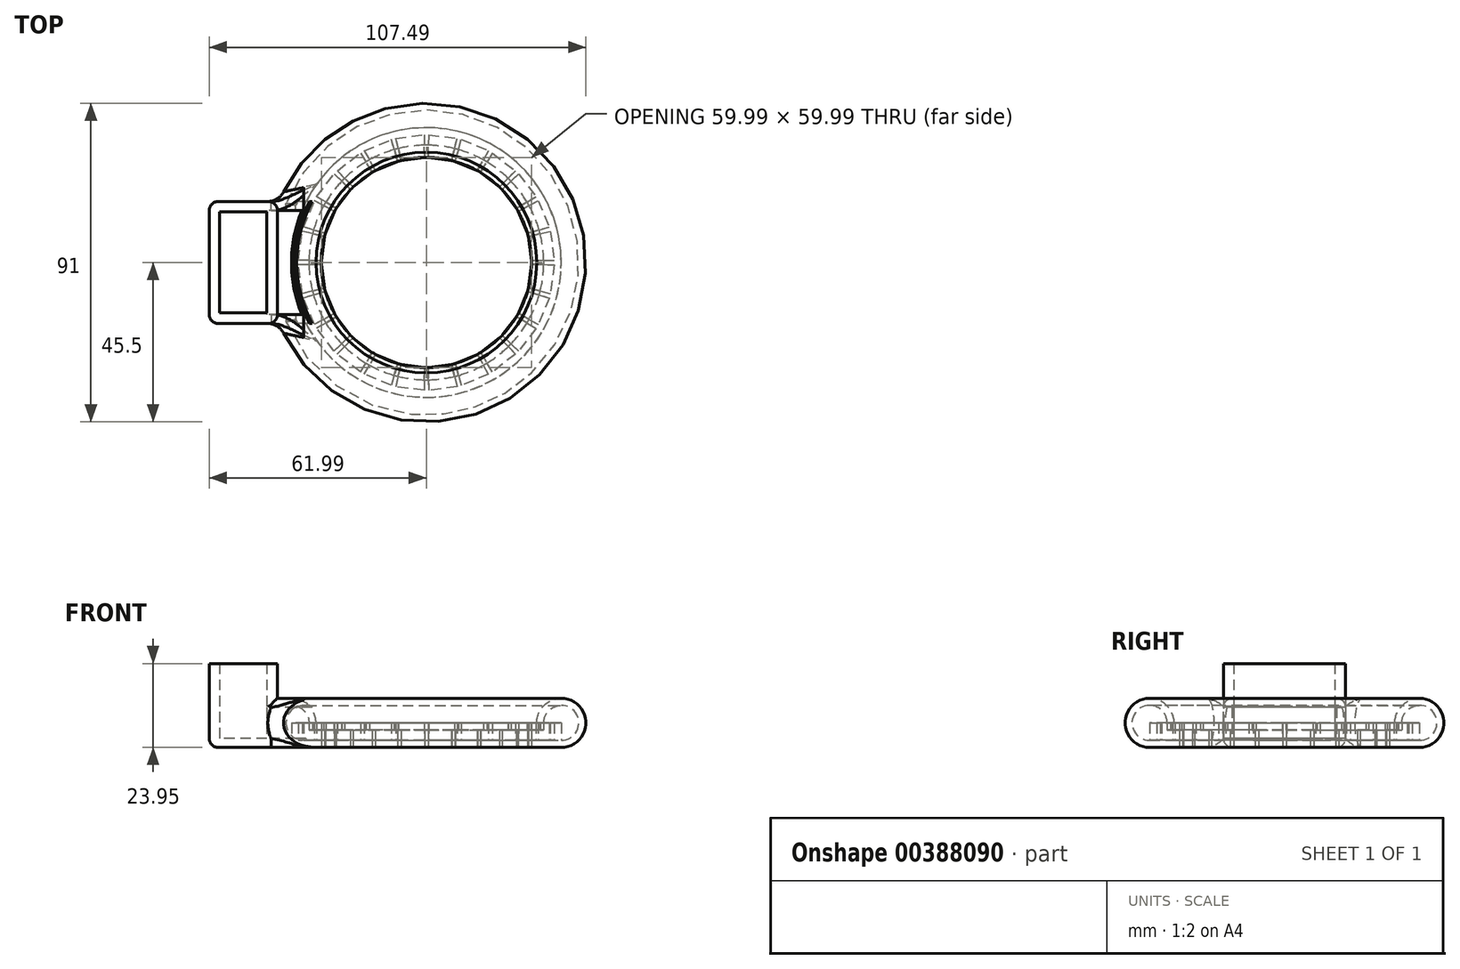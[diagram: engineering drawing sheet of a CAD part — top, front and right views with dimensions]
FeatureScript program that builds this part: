
annotation { "Feature Type Name" : "Feature", "Feature Type Description" : "" }
export const myFeature = defineFeature(function(context is Context, id is Id, definition is map)
    precondition{}
    {
        {
            var Q0;
            Q0=qCreatedBy(makeId("Right.planeOp"),FACE);
            cPlane(context, id + "F0", {"entities" : qUnion([Q0]), "cplaneType" : CPlaneType.OFFSET, "offset" : 45.5 * mm, "width" : 150 * mm, "height" : 150 * mm});
        }
        {
            var Q0;
            Q0=qCreatedBy(makeId("Front.planeOp"),FACE);
            cPlane(context, id + "F1", {"entities" : qUnion([Q0]), "cplaneType" : CPlaneType.OFFSET, "offset" : 17.41 * mm, "width" : 150 * mm, "height" : 150 * mm});
        }
        {
            var Q0;
            Q0=qCreatedBy(makeId("Front.planeOp"),FACE);
            cPlane(context, id + "F2", {"entities" : qUnion([Q0]), "cplaneType" : CPlaneType.OFFSET, "offset" : 17.41 * mm, "oppositeDirection" : true, "width" : 150 * mm, "height" : 150 * mm});
        }
        {
            var Q0;
            Q0=qCreatedBy(makeId("Top.planeOp"),FACE);
            cPlane(context, id + "F3", {"entities" : qUnion([Q0]), "cplaneType" : CPlaneType.OFFSET, "offset" : 7 * mm, "width" : 150 * mm, "height" : 150 * mm});
        }
        {
            var Q0;
            Q0=qCreatedBy(id+"F3.planeOp",FACE);
            cPlane(context, id + "F4", {"entities" : qUnion([Q0]), "cplaneType" : CPlaneType.OFFSET, "offset" : 6.95 * mm, "width" : 150 * mm, "height" : 150 * mm});
        }
        {
            var Q0;
            Q0=qCreatedBy(makeId("Top.planeOp"),FACE);
            var sketch = newSketch(context, id + "F5", { "sketchPlane" : qUnion([Q0])});
            skCircle(sketch, "E0", {"center": v(0, 0) * mm, "radius": 45 * mm});
            skCircle(sketch, "E1.0", {"center": v(0, 0) * mm, "radius": 38.5 * mm});
            skLineSegment(sketch, "E2", {"start": v(-136.41, 41.5) * mm, "end": v(-136.41, 35) * mm});
            skLineSegment(sketch, "E3", {"start": v(-128.72, 34) * mm, "end": v(-127.05, 40.28) * mm});
            skLineSegment(sketch, "E4", {"start": v(-118.16, 36.6) * mm, "end": v(-121.4, 30.99) * mm});
            skLineSegment(sketch, "E5", {"start": v(-115.15, 26.17) * mm, "end": v(-110.55, 30.76) * mm});
            skLineSegment(sketch, "E6", {"start": v(-110.44, 20.01) * mm, "end": v(-104.8, 23.26) * mm});
            skLineSegment(sketch, "E7", {"start": v(-107.45, 12.84) * mm, "end": v(-101.18, 14.54) * mm});
            skLineSegment(sketch, "E8", {"start": v(-106.41, 5.01) * mm, "end": v(-99.91, 5.01) * mm});
            skLineSegment(sketch, "E9.MirrorCS", {"start": v(-107.44, -2.81) * mm, "end": v(-101.17, -4.5) * mm});
            skLineSegment(sketch, "E10.MirrorCS", {"start": v(-110.42, -9.99) * mm, "end": v(-104.8, -13.24) * mm});
            skLineSegment(sketch, "E11.MirrorCS", {"start": v(-115.13, -16.15) * mm, "end": v(-110.52, -20.73) * mm});
            skLineSegment(sketch, "E12.MirrorCS", {"start": v(-118.13, -26.6) * mm, "end": v(-121.38, -20.97) * mm});
            skLineSegment(sketch, "E13.MirrorCS", {"start": v(-128.7, -24) * mm, "end": v(-127.02, -30.27) * mm});
            skLineSegment(sketch, "E14.MirrorCS", {"start": v(-144.1, 34) * mm, "end": v(-145.77, 40.28) * mm});
            skLineSegment(sketch, "E15.MirrorCS", {"start": v(-154.66, 36.6) * mm, "end": v(-151.41, 30.99) * mm});
            skLineSegment(sketch, "E16.MirrorCS", {"start": v(-157.67, 26.17) * mm, "end": v(-162.27, 30.76) * mm});
            skLineSegment(sketch, "E17.MirrorCS", {"start": v(-162.38, 20.01) * mm, "end": v(-168.01, 23.26) * mm});
            skLineSegment(sketch, "E18.MirrorCS", {"start": v(-165.37, 12.84) * mm, "end": v(-171.64, 14.54) * mm});
            skLineSegment(sketch, "E19.MirrorCS", {"start": v(-165.38, -2.81) * mm, "end": v(-171.65, -4.5) * mm});
            skLineSegment(sketch, "E20.MirrorCS", {"start": v(-162.4, -9.99) * mm, "end": v(-168.03, -13.24) * mm});
            skLineSegment(sketch, "E21.MirrorCS", {"start": v(-157.69, -16.15) * mm, "end": v(-162.3, -20.73) * mm});
            skLineSegment(sketch, "E22.MirrorCS", {"start": v(-154.69, -26.6) * mm, "end": v(-151.44, -20.97) * mm});
            skLineSegment(sketch, "E23.MirrorCS", {"start": v(-144.13, -24) * mm, "end": v(-145.8, -30.27) * mm});
            skLineSegment(sketch, "E24", {"start": v(-136.41, -25) * mm, "end": v(-136.41, -31.5) * mm});
            skLineSegment(sketch, "E25", {"start": v(-166.41, 5) * mm, "end": v(-172.91, 5) * mm});
            skCircle(sketch, "E26", {"center": v(-136.41, 5) * mm, "radius": 1.25 * mm, "construction": true});
            skLineSegment(sketch, "E27", {"start": v(0.64, 36.5) * mm, "end": v(0.52, 30) * mm});
            skLineSegment(sketch, "E28", {"start": v(8.2, 28.86) * mm, "end": v(9.97, 35.11) * mm});
            skLineSegment(sketch, "E29", {"start": v(18.8, 31.29) * mm, "end": v(15.46, 25.72) * mm});
            skLineSegment(sketch, "E30", {"start": v(21.62, 20.8) * mm, "end": v(26.3, 25.3) * mm});
            skLineSegment(sketch, "E31", {"start": v(26.23, 14.56) * mm, "end": v(31.92, 17.71) * mm});
            skLineSegment(sketch, "E32", {"start": v(29.1, 7.33) * mm, "end": v(35.4, 8.92) * mm});
            skLineSegment(sketch, "E33", {"start": v(30, -0.5) * mm, "end": v(36.5, -0.62) * mm});
            skLineSegment(sketch, "E34.MirrorCS", {"start": v(28.82, -8.32) * mm, "end": v(35.07, -10.12) * mm});
            skLineSegment(sketch, "E35.MirrorCS", {"start": v(25.72, -15.44) * mm, "end": v(31.3, -18.78) * mm});
            skLineSegment(sketch, "E36.MirrorCS", {"start": v(20.9, -21.52) * mm, "end": v(25.43, -26.18) * mm});
            skLineSegment(sketch, "E37.MirrorCS", {"start": v(17.73, -31.9) * mm, "end": v(14.57, -26.23) * mm});
            skLineSegment(sketch, "E38.MirrorCS", {"start": v(7.21, -29.12) * mm, "end": v(8.77, -35.43) * mm});
            skLineSegment(sketch, "E39.MirrorCS", {"start": v(-7.18, 29.13) * mm, "end": v(-8.74, 35.44) * mm});
            skLineSegment(sketch, "E40.MirrorCS", {"start": v(-17.7, 31.92) * mm, "end": v(-14.55, 26.25) * mm});
            skLineSegment(sketch, "E41.MirrorCS", {"start": v(-20.88, 21.54) * mm, "end": v(-25.4, 26.2) * mm});
            skLineSegment(sketch, "E42.MirrorCS", {"start": v(-25.7, 15.46) * mm, "end": v(-31.28, 18.81) * mm});
            skLineSegment(sketch, "E43.MirrorCS", {"start": v(-28.82, 8.34) * mm, "end": v(-35.06, 10.15) * mm});
            skLineSegment(sketch, "E44.MirrorCS", {"start": v(-29.1, -7.3) * mm, "end": v(-35.4, -8.89) * mm});
            skLineSegment(sketch, "E45.MirrorCS", {"start": v(-26.25, -14.53) * mm, "end": v(-31.93, -17.68) * mm});
            skLineSegment(sketch, "E46.MirrorCS", {"start": v(-21.64, -20.77) * mm, "end": v(-26.33, -25.28) * mm});
            skLineSegment(sketch, "E47.MirrorCS", {"start": v(-18.83, -31.27) * mm, "end": v(-15.48, -25.7) * mm});
            skLineSegment(sketch, "E48.MirrorCS", {"start": v(-8.22, -28.85) * mm, "end": v(-10, -35.1) * mm});
            skLineSegment(sketch, "E49", {"start": v(-0.52, -30) * mm, "end": v(-0.64, -36.5) * mm});
            skLineSegment(sketch, "E50", {"start": v(-30, 0.52) * mm, "end": v(-36.5, 0.64) * mm});
            skLineSegment(sketch, "E51", {"start": v(-0.64, 36.5) * mm, "end": v(-0.52, 30) * mm});
            skLineSegment(sketch, "E52", {"start": v(7.18, 29.13) * mm, "end": v(8.74, 35.44) * mm});
            skLineSegment(sketch, "E53", {"start": v(17.7, 31.92) * mm, "end": v(14.55, 26.25) * mm});
            skLineSegment(sketch, "E54", {"start": v(20.88, 21.54) * mm, "end": v(25.4, 26.2) * mm});
            skLineSegment(sketch, "E55", {"start": v(25.7, 15.46) * mm, "end": v(31.28, 18.81) * mm});
            skLineSegment(sketch, "E56", {"start": v(28.82, 8.34) * mm, "end": v(35.06, 10.15) * mm});
            skLineSegment(sketch, "E57", {"start": v(30, 0.54) * mm, "end": v(36.5, 0.65) * mm});
            skLineSegment(sketch, "E58.MirrorCS", {"start": v(29.1, -7.3) * mm, "end": v(35.4, -8.89) * mm});
            skLineSegment(sketch, "E59.MirrorCS", {"start": v(26.25, -14.53) * mm, "end": v(31.93, -17.68) * mm});
            skLineSegment(sketch, "E60.MirrorCS", {"start": v(21.64, -20.77) * mm, "end": v(26.33, -25.28) * mm});
            skLineSegment(sketch, "E61.MirrorCS", {"start": v(18.83, -31.27) * mm, "end": v(15.48, -25.7) * mm});
            skLineSegment(sketch, "E62.MirrorCS", {"start": v(8.22, -28.85) * mm, "end": v(10, -35.1) * mm});
            skLineSegment(sketch, "E63.MirrorCS", {"start": v(-8.2, 28.86) * mm, "end": v(-9.97, 35.11) * mm});
            skLineSegment(sketch, "E64.MirrorCS", {"start": v(-18.8, 31.29) * mm, "end": v(-15.46, 25.72) * mm});
            skLineSegment(sketch, "E65.MirrorCS", {"start": v(-21.62, 20.8) * mm, "end": v(-26.3, 25.3) * mm});
            skLineSegment(sketch, "E66.MirrorCS", {"start": v(-26.23, 14.56) * mm, "end": v(-31.92, 17.71) * mm});
            skLineSegment(sketch, "E67.MirrorCS", {"start": v(-29.1, 7.33) * mm, "end": v(-35.4, 8.92) * mm});
            skLineSegment(sketch, "E68.MirrorCS", {"start": v(-28.82, -8.32) * mm, "end": v(-35.07, -10.12) * mm});
            skLineSegment(sketch, "E69.MirrorCS", {"start": v(-25.72, -15.44) * mm, "end": v(-31.3, -18.78) * mm});
            skLineSegment(sketch, "E70.MirrorCS", {"start": v(-20.9, -21.52) * mm, "end": v(-25.43, -26.18) * mm});
            skLineSegment(sketch, "E71.MirrorCS", {"start": v(-17.73, -31.9) * mm, "end": v(-14.57, -26.23) * mm});
            skLineSegment(sketch, "E72.MirrorCS", {"start": v(-7.21, -29.12) * mm, "end": v(-8.77, -35.43) * mm});
            skLineSegment(sketch, "E73", {"start": v(0.52, -30) * mm, "end": v(0.64, -36.5) * mm});
            skLineSegment(sketch, "E74", {"start": v(-30, -0.52) * mm, "end": v(-36.5, -0.64) * mm});
            skCircle(sketch, "E75", {"center": v(0, 0) * mm, "radius": 1.25 * mm, "construction": true});
            skLineSegment(sketch, "E76", {"start": v(-29.1, 7.33) * mm, "end": v(-28.82, 8.34) * mm});
            skLineSegment(sketch, "E77", {"start": v(-28.82, 8.34) * mm, "end": v(-26.23, 14.56) * mm});
            skLineSegment(sketch, "E78", {"start": v(-26.23, 14.56) * mm, "end": v(-25.7, 15.46) * mm});
            skLineSegment(sketch, "E79", {"start": v(-25.7, 15.46) * mm, "end": v(-21.62, 20.8) * mm});
            skLineSegment(sketch, "E80", {"start": v(-21.62, 20.8) * mm, "end": v(-20.88, 21.54) * mm});
            skLineSegment(sketch, "E81", {"start": v(-20.88, 21.54) * mm, "end": v(-15.46, 25.72) * mm});
            skLineSegment(sketch, "E82", {"start": v(-15.46, 25.72) * mm, "end": v(-14.55, 26.25) * mm});
            skLineSegment(sketch, "E83", {"start": v(-14.55, 26.25) * mm, "end": v(-8.2, 28.86) * mm});
            skLineSegment(sketch, "E84", {"start": v(-8.2, 28.86) * mm, "end": v(-7.18, 29.13) * mm});
            skLineSegment(sketch, "E85", {"start": v(-7.18, 29.13) * mm, "end": v(-0.52, 30) * mm});
            skLineSegment(sketch, "E86", {"start": v(-0.52, 30) * mm, "end": v(0.52, 30) * mm});
            skLineSegment(sketch, "E87", {"start": v(0.52, 30) * mm, "end": v(7.18, 29.13) * mm});
            skLineSegment(sketch, "E88", {"start": v(7.18, 29.13) * mm, "end": v(8.2, 28.86) * mm});
            skLineSegment(sketch, "E89", {"start": v(8.2, 28.86) * mm, "end": v(14.55, 26.25) * mm});
            skLineSegment(sketch, "E90", {"start": v(14.55, 26.25) * mm, "end": v(15.46, 25.72) * mm});
            skLineSegment(sketch, "E91", {"start": v(15.46, 25.72) * mm, "end": v(20.88, 21.54) * mm});
            skLineSegment(sketch, "E92", {"start": v(20.88, 21.54) * mm, "end": v(21.62, 20.8) * mm});
            skLineSegment(sketch, "E93", {"start": v(21.62, 20.8) * mm, "end": v(25.7, 15.46) * mm});
            skLineSegment(sketch, "E94", {"start": v(25.7, 15.46) * mm, "end": v(26.23, 14.56) * mm});
            skLineSegment(sketch, "E95", {"start": v(26.23, 14.56) * mm, "end": v(28.82, 8.34) * mm});
            skLineSegment(sketch, "E96", {"start": v(28.82, 8.34) * mm, "end": v(29.1, 7.33) * mm});
            skLineSegment(sketch, "E97", {"start": v(29.1, 7.33) * mm, "end": v(30, 0.54) * mm});
            skLineSegment(sketch, "E98", {"start": v(30, 0.54) * mm, "end": v(30, -0.5) * mm});
            skLineSegment(sketch, "E99", {"start": v(30, -0.5) * mm, "end": v(29.1, -7.3) * mm});
            skLineSegment(sketch, "E100", {"start": v(29.1, -7.3) * mm, "end": v(28.82, -8.32) * mm});
            skLineSegment(sketch, "E101", {"start": v(28.82, -8.32) * mm, "end": v(26.25, -14.53) * mm});
            skLineSegment(sketch, "E102", {"start": v(26.25, -14.53) * mm, "end": v(25.72, -15.44) * mm});
            skLineSegment(sketch, "E103", {"start": v(25.72, -15.44) * mm, "end": v(21.64, -20.77) * mm});
            skLineSegment(sketch, "E104", {"start": v(21.64, -20.77) * mm, "end": v(20.9, -21.52) * mm});
            skLineSegment(sketch, "E105", {"start": v(20.9, -21.52) * mm, "end": v(15.48, -25.7) * mm});
            skLineSegment(sketch, "E106", {"start": v(15.48, -25.7) * mm, "end": v(14.57, -26.23) * mm});
            skLineSegment(sketch, "E107", {"start": v(14.57, -26.23) * mm, "end": v(8.22, -28.85) * mm});
            skLineSegment(sketch, "E108", {"start": v(8.22, -28.85) * mm, "end": v(7.21, -29.12) * mm});
            skLineSegment(sketch, "E109", {"start": v(7.21, -29.12) * mm, "end": v(0.52, -30) * mm});
            skLineSegment(sketch, "E110", {"start": v(0.52, -30) * mm, "end": v(-0.52, -30) * mm});
            skLineSegment(sketch, "E111", {"start": v(-0.52, -30) * mm, "end": v(-7.21, -29.12) * mm});
            skLineSegment(sketch, "E112", {"start": v(-7.21, -29.12) * mm, "end": v(-8.22, -28.85) * mm});
            skLineSegment(sketch, "E113", {"start": v(-8.22, -28.85) * mm, "end": v(-14.57, -26.23) * mm});
            skLineSegment(sketch, "E114", {"start": v(-14.57, -26.23) * mm, "end": v(-15.48, -25.7) * mm});
            skLineSegment(sketch, "E115", {"start": v(-15.48, -25.7) * mm, "end": v(-20.9, -21.52) * mm});
            skLineSegment(sketch, "E116", {"start": v(-20.9, -21.52) * mm, "end": v(-21.64, -20.77) * mm});
            skLineSegment(sketch, "E117", {"start": v(-21.64, -20.77) * mm, "end": v(-25.72, -15.44) * mm});
            skLineSegment(sketch, "E118", {"start": v(-25.72, -15.44) * mm, "end": v(-26.25, -14.53) * mm});
            skLineSegment(sketch, "E119", {"start": v(-28.82, -8.32) * mm, "end": v(-29.1, -7.3) * mm});
            skLineSegment(sketch, "E120", {"start": v(-26.25, -14.53) * mm, "end": v(-28.82, -8.32) * mm});
            skLineSegment(sketch, "E121", {"start": v(-29.1, -7.3) * mm, "end": v(-30, -0.52) * mm});
            skLineSegment(sketch, "E122", {"start": v(-30, -0.52) * mm, "end": v(-30, 0.52) * mm});
            skLineSegment(sketch, "E123", {"start": v(-30, 0.52) * mm, "end": v(-29.1, 7.33) * mm});
            skLineSegment(sketch, "E124", {"start": v(-36.5, 0.64) * mm, "end": v(-35.4, 8.92) * mm});
            skLineSegment(sketch, "E125", {"start": v(-35.06, 10.15) * mm, "end": v(-31.92, 17.71) * mm});
            skLineSegment(sketch, "E126", {"start": v(-31.28, 18.81) * mm, "end": v(-26.3, 25.3) * mm});
            skLineSegment(sketch, "E127", {"start": v(-25.4, 26.2) * mm, "end": v(-18.8, 31.29) * mm});
            skLineSegment(sketch, "E128", {"start": v(-17.7, 31.92) * mm, "end": v(-9.97, 35.11) * mm});
            skLineSegment(sketch, "E129", {"start": v(-8.74, 35.44) * mm, "end": v(-0.64, 36.5) * mm});
            skLineSegment(sketch, "E130", {"start": v(0.64, 36.5) * mm, "end": v(8.74, 35.44) * mm});
            skLineSegment(sketch, "E131", {"start": v(9.97, 35.11) * mm, "end": v(17.7, 31.92) * mm});
            skLineSegment(sketch, "E132", {"start": v(18.8, 31.29) * mm, "end": v(25.4, 26.2) * mm});
            skLineSegment(sketch, "E133", {"start": v(26.3, 25.3) * mm, "end": v(31.28, 18.81) * mm});
            skLineSegment(sketch, "E134", {"start": v(31.92, 17.71) * mm, "end": v(35.06, 10.15) * mm});
            skLineSegment(sketch, "E135", {"start": v(35.4, 8.92) * mm, "end": v(36.5, 0.65) * mm});
            skLineSegment(sketch, "E136", {"start": v(36.5, -0.62) * mm, "end": v(35.4, -8.89) * mm});
            skLineSegment(sketch, "E137", {"start": v(35.07, -10.12) * mm, "end": v(31.93, -17.68) * mm});
            skLineSegment(sketch, "E138", {"start": v(31.3, -18.78) * mm, "end": v(26.33, -25.28) * mm});
            skLineSegment(sketch, "E139", {"start": v(25.43, -26.18) * mm, "end": v(18.83, -31.27) * mm});
            skLineSegment(sketch, "E140", {"start": v(17.73, -31.9) * mm, "end": v(10, -35.1) * mm});
            skLineSegment(sketch, "E141", {"start": v(8.77, -35.43) * mm, "end": v(0.64, -36.5) * mm});
            skLineSegment(sketch, "E142", {"start": v(-0.64, -36.5) * mm, "end": v(-8.77, -35.43) * mm});
            skLineSegment(sketch, "E143", {"start": v(-10, -35.1) * mm, "end": v(-17.73, -31.9) * mm});
            skLineSegment(sketch, "E144", {"start": v(-18.83, -31.27) * mm, "end": v(-25.43, -26.18) * mm});
            skLineSegment(sketch, "E145", {"start": v(-26.33, -25.28) * mm, "end": v(-31.3, -18.78) * mm});
            skLineSegment(sketch, "E146", {"start": v(-31.93, -17.68) * mm, "end": v(-35.07, -10.12) * mm});
            skLineSegment(sketch, "E147", {"start": v(-35.4, -8.89) * mm, "end": v(-36.5, -0.64) * mm});
            skSolve(sketch);
        }
        {
            var Q0;
            Q0=qCreatedBy(makeId("Front.planeOp"),FACE);
            var sketch = newSketch(context, id + "F6", { "sketchPlane" : qUnion([Q0])});
            skLineSegment(sketch, "E148.bottom", {"start": v(38.5, 7) * mm, "end": v(-38.5, 7) * mm, "construction": true});
            skLineSegment(sketch, "E148.top", {"start": v(38.5, -7) * mm, "end": v(-38.5, -7) * mm, "construction": true});
            skLineSegment(sketch, "E148.left", {"start": v(38.5, 7) * mm, "end": v(38.5, -7) * mm, "construction": true});
            skLineSegment(sketch, "E148.right", {"start": v(-38.5, 7) * mm, "end": v(-38.5, -7) * mm, "construction": true});
            skPoint(sketch, "E148.middle", {"position": v(0, 0) * mm});
            skLineSegment(sketch, "E149", {"start": v(-38.5, 0) * mm, "end": v(38.5, 0) * mm, "construction": true});
            skArc(sketch, "E150", {"start": v(38.5, 0) * mm, "mid": v(43.45, 11.95) * mm, "end": v(31.5, 7) * mm});
            skArc(sketch, "E151", {"start": v(38.5, 2) * mm, "mid": v(42.04, 10.54) * mm, "end": v(33.5, 7) * mm});
            skLineSegment(sketch, "E152", {"start": v(38.5, 2) * mm, "end": v(38.5, 0) * mm});
            skLineSegment(sketch, "E153", {"start": v(38.5, 2) * mm, "end": v(31.5, 2) * mm, "construction": true});
            skLineSegment(sketch, "E154", {"start": v(31.5, 2) * mm, "end": v(31.5, 0) * mm, "construction": true});
            skLineSegment(sketch, "E155.0", {"start": v(38.5, 5) * mm, "end": v(-38.5, 5) * mm, "construction": true});
            skLineSegment(sketch, "E156", {"start": v(30, 0) * mm, "end": v(30, 7) * mm, "construction": true});
            skLineSegment(sketch, "E157", {"start": v(31.5, 7) * mm, "end": v(30, 7) * mm});
            skLineSegment(sketch, "E158", {"start": v(30, 7) * mm, "end": v(30, 5) * mm});
            skLineSegment(sketch, "E159", {"start": v(30, 5) * mm, "end": v(33.5, 5) * mm});
            skLineSegment(sketch, "E160", {"start": v(33.5, 5) * mm, "end": v(33.5, 7) * mm});
            skLineSegment(sketch, "E161", {"start": v(0, -7) * mm, "end": v(0, 7) * mm, "construction": true});
            skLineSegment(sketch, "E162", {"start": v(38.5, 7) * mm, "end": v(38.5, 14) * mm, "construction": true});
            skLineSegment(sketch, "E163", {"start": v(38.5, 7) * mm, "end": v(45.5, 7) * mm, "construction": true});
            skLineSegment(sketch, "E164", {"start": v(38.5, 12) * mm, "end": v(38.5, 14) * mm});
            skLineSegment(sketch, "E165", {"start": v(43.5, 7) * mm, "end": v(45.5, 7) * mm});
            skLineSegment(sketch, "E166.MirrorCS", {"start": v(-38.5, 2) * mm, "end": v(-38.5, 0) * mm});
            skLineSegment(sketch, "E167.MirrorCS", {"start": v(-30, 7) * mm, "end": v(-30, 5) * mm});
            skLineSegment(sketch, "E168.MirrorCS", {"start": v(-31.5, 7) * mm, "end": v(-30, 7) * mm});
            skLineSegment(sketch, "E169.MirrorCS", {"start": v(-33.5, 5) * mm, "end": v(-33.5, 7) * mm});
            skLineSegment(sketch, "E170.MirrorCS", {"start": v(-43.5, 7) * mm, "end": v(-45.5, 7) * mm});
            skLineSegment(sketch, "E171.MirrorCS", {"start": v(-30, 5) * mm, "end": v(-33.5, 5) * mm});
            skLineSegment(sketch, "E172.MirrorCS", {"start": v(-31.5, 2) * mm, "end": v(-31.5, 0) * mm, "construction": true});
            skLineSegment(sketch, "E173.MirrorCS", {"start": v(-38.5, 12) * mm, "end": v(-38.5, 14) * mm});
            skLineSegment(sketch, "E174.MirrorCS", {"start": v(-38.5, 7) * mm, "end": v(-45.5, 7) * mm, "construction": true});
            skLineSegment(sketch, "E175.MirrorCS", {"start": v(-38.5, 2) * mm, "end": v(-31.5, 2) * mm, "construction": true});
            skLineSegment(sketch, "E176.MirrorCS", {"start": v(-38.5, 7) * mm, "end": v(-38.5, 14) * mm, "construction": true});
            skArc(sketch, "E177.MirrorCS", {"start": v(-38.5, 0) * mm, "mid": v(-43.45, 11.95) * mm, "end": v(-31.5, 7) * mm});
            skArc(sketch, "E178.MirrorCS", {"start": v(-38.5, 2) * mm, "mid": v(-42.04, 10.54) * mm, "end": v(-33.5, 7) * mm});
            skLineSegment(sketch, "E179.MirrorCS", {"start": v(-38.5, 5) * mm, "end": v(38.5, 5) * mm, "construction": true});
            skLineSegment(sketch, "E180.MirrorCS", {"start": v(-30, 0) * mm, "end": v(-30, 7) * mm, "construction": true});
            skLineSegment(sketch, "E181.MirrorCS", {"start": v(-38.5, 7) * mm, "end": v(38.5, 7) * mm, "construction": true});
            skSolve(sketch);
        }
        {
            var Q0;
            Q0=qCreatedBy(id+"F1.planeOp",FACE);
            var sketch = newSketch(context, id + "F7", { "sketchPlane" : qUnion([Q0])});
            skLineSegment(sketch, "E182.bottom", {"start": v(45.5, 14) * mm, "end": v(-45.5, 14) * mm, "construction": true});
            skLineSegment(sketch, "E182.top", {"start": v(45.5, -14) * mm, "end": v(-45.5, -14) * mm, "construction": true});
            skLineSegment(sketch, "E182.left", {"start": v(45.5, 14) * mm, "end": v(45.5, -14) * mm, "construction": true});
            skLineSegment(sketch, "E182.right", {"start": v(-45.5, 14) * mm, "end": v(-45.5, -14) * mm, "construction": true});
            skPoint(sketch, "E182.middle", {"position": v(0, 0) * mm});
            skLineSegment(sketch, "E183", {"start": v(-45.5, 0) * mm, "end": v(45.5, 0) * mm, "construction": true});
            skLineSegment(sketch, "E184", {"start": v(0, 14) * mm, "end": v(0, -14) * mm, "construction": true});
            skLineSegment(sketch, "E185.0", {"start": v(-17.41, 14) * mm, "end": v(-17.41, -14) * mm, "construction": true});
            skLineSegment(sketch, "E186.MirrorCS", {"start": v(17.41, 14) * mm, "end": v(17.41, -14) * mm, "construction": true});
            skLineSegment(sketch, "E187.0", {"start": v(45.5, 7) * mm, "end": v(-45.5, 7) * mm, "construction": true});
            skLineSegment(sketch, "E188", {"start": v(-17.41, 14) * mm, "end": v(-17.41, 7) * mm});
            skLineSegment(sketch, "E189", {"start": v(-17.41, 7) * mm, "end": v(17.41, 7) * mm});
            skLineSegment(sketch, "E190", {"start": v(17.41, 7) * mm, "end": v(17.41, 14) * mm});
            skLineSegment(sketch, "E191", {"start": v(17.41, 14) * mm, "end": v(-17.41, 14) * mm});
            skLineSegment(sketch, "E192.0", {"start": v(45.5, 12) * mm, "end": v(-45.5, 12) * mm, "construction": true});
            skLineSegment(sketch, "E193.0", {"start": v(-14.73, 14) * mm, "end": v(-14.73, -14) * mm, "construction": true});
            skLineSegment(sketch, "E194.MirrorCS", {"start": v(14.73, 14) * mm, "end": v(14.73, -14) * mm, "construction": true});
            skLineSegment(sketch, "E195", {"start": v(-14.73, 7) * mm, "end": v(-14.73, 14) * mm});
            skLineSegment(sketch, "E196", {"start": v(14.73, 7) * mm, "end": v(14.73, 14) * mm});
            skLineSegment(sketch, "E197", {"start": v(17.41, 12) * mm, "end": v(-17.41, 12) * mm});
            skPoint(sketch, "E197.startSnap0", {"position": v(17.41, 10.5) * mm});
            skLineSegment(sketch, "E198", {"start": v(45.5, 14) * mm, "end": v(45.5, 7) * mm});
            skCircle(sketch, "E199", {"center": v(-35.07, 7) * mm, "radius": 7 * mm, "construction": true});
            skArc(sketch, "E200", {"start": v(-35.07, 12) * mm, "mid": v(-40.07, 7) * mm, "end": v(-35.07, 2) * mm});
            skLineSegment(sketch, "E201", {"start": v(-35.07, 12) * mm, "end": v(-35.07, 14) * mm});
            skLineSegment(sketch, "E202", {"start": v(-35.07, 14) * mm, "end": v(-45.5, 14) * mm});
            skLineSegment(sketch, "E203", {"start": v(-45.5, 14) * mm, "end": v(-45.5, 0) * mm});
            skLineSegment(sketch, "E204", {"start": v(-45.5, 0) * mm, "end": v(-35.07, 0) * mm});
            skLineSegment(sketch, "E205", {"start": v(-35.07, 0) * mm, "end": v(-35.07, 2) * mm});
            skLineSegment(sketch, "E206.MirrorCS", {"start": v(45.5, 2) * mm, "end": v(-45.5, 2) * mm, "construction": true});
            skCircle(sketch, "E207", {"center": v(0, 7) * mm, "radius": 1.25 * mm, "construction": true});
            skSolve(sketch);
        }
        {
            var Q0;
            Q0=qCreatedBy(id+"F2.planeOp",FACE);
            var sketch = newSketch(context, id + "F8", { "sketchPlane" : qUnion([Q0])});
            skLineSegment(sketch, "E208.bottom", {"start": v(45.5, 14) * mm, "end": v(-45.5, 14) * mm, "construction": true});
            skLineSegment(sketch, "E208.top", {"start": v(45.5, -14) * mm, "end": v(-45.5, -14) * mm, "construction": true});
            skLineSegment(sketch, "E208.left", {"start": v(45.5, 14) * mm, "end": v(45.5, -14) * mm, "construction": true});
            skLineSegment(sketch, "E208.right", {"start": v(-45.5, 14) * mm, "end": v(-45.5, -14) * mm, "construction": true});
            skPoint(sketch, "E208.middle", {"position": v(0, 0) * mm});
            skLineSegment(sketch, "E209", {"start": v(-45.5, 0) * mm, "end": v(45.5, 0) * mm, "construction": true});
            skLineSegment(sketch, "E210", {"start": v(0, 14) * mm, "end": v(0, -14) * mm, "construction": true});
            skLineSegment(sketch, "E211.0", {"start": v(-17.41, 14) * mm, "end": v(-17.41, -14) * mm, "construction": true});
            skLineSegment(sketch, "E212.MirrorCS", {"start": v(17.41, 14) * mm, "end": v(17.41, -14) * mm, "construction": true});
            skLineSegment(sketch, "E213.0", {"start": v(45.5, 7) * mm, "end": v(-45.5, 7) * mm, "construction": true});
            skLineSegment(sketch, "E214", {"start": v(-17.41, 14) * mm, "end": v(-17.41, 7) * mm});
            skLineSegment(sketch, "E215", {"start": v(-17.41, 7) * mm, "end": v(17.41, 7) * mm});
            skLineSegment(sketch, "E216", {"start": v(17.41, 7) * mm, "end": v(17.41, 14) * mm});
            skLineSegment(sketch, "E217", {"start": v(17.41, 14) * mm, "end": v(-17.41, 14) * mm});
            skLineSegment(sketch, "E218.0", {"start": v(45.5, 12) * mm, "end": v(-45.5, 12) * mm, "construction": true});
            skLineSegment(sketch, "E219.0", {"start": v(-14.73, 14) * mm, "end": v(-14.73, -14) * mm, "construction": true});
            skLineSegment(sketch, "E220.MirrorCS", {"start": v(14.73, 14) * mm, "end": v(14.73, -14) * mm, "construction": true});
            skLineSegment(sketch, "E221", {"start": v(-14.73, 7) * mm, "end": v(-14.73, 14) * mm});
            skLineSegment(sketch, "E222", {"start": v(14.73, 7) * mm, "end": v(14.73, 14) * mm});
            skLineSegment(sketch, "E223", {"start": v(17.41, 12) * mm, "end": v(-17.41, 12) * mm});
            skPoint(sketch, "E223.startSnap0", {"position": v(17.41, 10.5) * mm});
            skLineSegment(sketch, "E224", {"start": v(45.5, 14) * mm, "end": v(45.5, 7) * mm});
            skCircle(sketch, "E225", {"center": v(-35.07, 7) * mm, "radius": 7 * mm, "construction": true});
            skArc(sketch, "E226", {"start": v(-35.07, 12) * mm, "mid": v(-40.07, 7) * mm, "end": v(-35.07, 2) * mm});
            skLineSegment(sketch, "E227", {"start": v(-35.07, 12) * mm, "end": v(-35.07, 14) * mm});
            skLineSegment(sketch, "E228", {"start": v(-35.07, 14) * mm, "end": v(-45.5, 14) * mm});
            skLineSegment(sketch, "E229", {"start": v(-45.5, 14) * mm, "end": v(-45.5, 0) * mm});
            skLineSegment(sketch, "E230", {"start": v(-45.5, 0) * mm, "end": v(-35.07, 0) * mm});
            skLineSegment(sketch, "E231", {"start": v(-35.07, 0) * mm, "end": v(-35.07, 2) * mm});
            skLineSegment(sketch, "E232.MirrorCS", {"start": v(45.5, 2) * mm, "end": v(-45.5, 2) * mm, "construction": true});
            skCircle(sketch, "E233", {"center": v(0, 7) * mm, "radius": 1.25 * mm, "construction": true});
            skSolve(sketch);
        }
        {
            var Q0;
            Q0=qCreatedBy(makeId("Top.planeOp"),FACE);
            var sketch = newSketch(context, id + "F9", { "sketchPlane" : qUnion([Q0])});
            skPoint(sketch, "E234.middle", {"position": v(0, 0) * mm});
            skCircle(sketch, "E235", {"center": v(0, 0) * mm, "radius": 2.5 * mm, "construction": true});
            skLineSegment(sketch, "E236.MirrorCS", {"start": v(-32.65, 17.41) * mm, "end": v(-45.5, 17.41) * mm});
            skLineSegment(sketch, "E237.MirrorCS", {"start": v(-32.65, -17.41) * mm, "end": v(-45.5, -17.41) * mm});
            skLineSegment(sketch, "E238.MirrorCS", {"start": v(-45.5, 17.41) * mm, "end": v(-45.5, -17.41) * mm});
            skArc(sketch, "E239", {"start": v(-32.65, 17.41) * mm, "mid": v(-37, 0) * mm, "end": v(-32.65, -17.41) * mm});
            skLineSegment(sketch, "E240.bottom", {"start": v(-45.5, 8.28) * mm, "end": v(-45.5, -8.52) * mm, "construction": true});
            skLineSegment(sketch, "E240.left", {"start": v(-45.5, 8.28) * mm, "end": v(-59, 8.28) * mm, "construction": true});
            skLineSegment(sketch, "E241", {"start": v(-45.5, -8.52) * mm, "end": v(-59, -8.52) * mm, "construction": true});
            skLineSegment(sketch, "E242", {"start": v(-59, -8.52) * mm, "end": v(-59, 8.28) * mm, "construction": true});
            skLineSegment(sketch, "E243", {"start": v(-45.5, 8.28) * mm, "end": v(-59, -8.52) * mm, "construction": true});
            skLineSegment(sketch, "E244", {"start": v(-45.5, -8.52) * mm, "end": v(-59, 8.28) * mm, "construction": true});
            skLineSegment(sketch, "E245", {"start": v(-52.24, 0) * mm, "end": v(-42.5, 0) * mm, "construction": true});
            skLineSegment(sketch, "E246", {"start": v(-27.2, 0) * mm, "end": v(-42.4, 0) * mm, "construction": true});
            skLineSegment(sketch, "E247.0", {"start": v(-62, -8.52) * mm, "end": v(-62, 8.28) * mm, "construction": true});
            skLineSegment(sketch, "E248", {"start": v(-45.5, 17.41) * mm, "end": v(-62, 17.41) * mm});
            skLineSegment(sketch, "E249", {"start": v(-62, 17.41) * mm, "end": v(-62, -17.41) * mm});
            skLineSegment(sketch, "E250", {"start": v(-62, -17.41) * mm, "end": v(-45.5, -17.41) * mm});
            skLineSegment(sketch, "E251.0", {"start": v(-59, -14.41) * mm, "end": v(-45.5, -14.41) * mm});
            skLineSegment(sketch, "E251.1", {"start": v(-59, 14.41) * mm, "end": v(-59, -14.41) * mm});
            skLineSegment(sketch, "E251.2", {"start": v(-45.5, 14.41) * mm, "end": v(-59, 14.41) * mm});
            skSolve(sketch);
        }
        {
            var Q0;
            Q0=qCreatedBy(id+"F4.planeOp",FACE);
            var sketch = newSketch(context, id + "F10", { "sketchPlane" : qUnion([Q0])});
            skPoint(sketch, "E252.middle", {"position": v(0, 0) * mm});
            skCircle(sketch, "E253", {"center": v(0, 0) * mm, "radius": 2.5 * mm, "construction": true});
            skLineSegment(sketch, "E254.MirrorCS", {"start": v(-32.65, 17.41) * mm, "end": v(-45.5, 17.41) * mm});
            skLineSegment(sketch, "E255.MirrorCS", {"start": v(-32.65, -17.41) * mm, "end": v(-45.5, -17.41) * mm});
            skLineSegment(sketch, "E256.MirrorCS", {"start": v(-45.5, 17.41) * mm, "end": v(-45.5, -17.41) * mm});
            skArc(sketch, "E257", {"start": v(-32.65, 17.41) * mm, "mid": v(-37, 0) * mm, "end": v(-32.65, -17.41) * mm});
            skLineSegment(sketch, "E258.bottom", {"start": v(-45.5, 8.28) * mm, "end": v(-45.5, -8.52) * mm, "construction": true});
            skLineSegment(sketch, "E258.left", {"start": v(-45.5, 8.28) * mm, "end": v(-59, 8.28) * mm, "construction": true});
            skLineSegment(sketch, "E259", {"start": v(-45.5, -8.52) * mm, "end": v(-59, -8.52) * mm, "construction": true});
            skLineSegment(sketch, "E260", {"start": v(-59, -8.52) * mm, "end": v(-59, 8.28) * mm, "construction": true});
            skLineSegment(sketch, "E261", {"start": v(-45.5, 8.28) * mm, "end": v(-59, -8.52) * mm, "construction": true});
            skLineSegment(sketch, "E262", {"start": v(-45.5, -8.52) * mm, "end": v(-59, 8.28) * mm, "construction": true});
            skLineSegment(sketch, "E263", {"start": v(-52.24, 0) * mm, "end": v(-42.5, 0) * mm, "construction": true});
            skLineSegment(sketch, "E264", {"start": v(-27.2, 0) * mm, "end": v(-42.4, 0) * mm, "construction": true});
            skLineSegment(sketch, "E265.0", {"start": v(-62, -8.52) * mm, "end": v(-62, 8.28) * mm, "construction": true});
            skLineSegment(sketch, "E266", {"start": v(-45.5, 17.41) * mm, "end": v(-62, 17.41) * mm});
            skLineSegment(sketch, "E267", {"start": v(-62, 17.41) * mm, "end": v(-62, -17.41) * mm});
            skLineSegment(sketch, "E268", {"start": v(-62, -17.41) * mm, "end": v(-45.5, -17.41) * mm});
            skLineSegment(sketch, "E269.0", {"start": v(-59, -14.41) * mm, "end": v(-45.5, -14.41) * mm});
            skLineSegment(sketch, "E269.1", {"start": v(-59, 14.41) * mm, "end": v(-59, -14.41) * mm});
            skLineSegment(sketch, "E269.2", {"start": v(-45.5, 14.41) * mm, "end": v(-59, 14.41) * mm});
            skLineSegment(sketch, "E270.0", {"start": v(-42.5, 17.41) * mm, "end": v(-42.5, -17.41) * mm});
            skSolve(sketch);
        }
        {
            var Q0;
            Q0=makeQuery(id+"F5.imprint","IMPRINT",FACE,{"disambiguationData":[TD([[makeQuery(id+"F5.imprint","IMPRINT",EDGE,{"derivedFrom":sQuery(id+"F5.wireOp",EDGE,"E1.0")}),1.0]])]});
            extrude(context, id + "F11", {"entities" : qUnion([Q0]), "depth" : 7 * mm});
        }
        {
            var Q0;
            Q0=makeQuery(id+"F5.imprint","IMPRINT",FACE,{"disambiguationData":[TD([[makeQuery(id+"F5.imprint","IMPRINT",EDGE,{"derivedFrom":sQuery(id+"F5.wireOp",EDGE,"E50")}),-1.0]])]});
            var Q1;
            Q1=makeQuery(id+"F5.imprint","IMPRINT",FACE,{"disambiguationData":[TD([[makeQuery(id+"F5.imprint","IMPRINT",EDGE,{"derivedFrom":sQuery(id+"F5.wireOp",EDGE,"E43.MirrorCS")}),-1.0]])]});
            var Q2;
            Q2=makeQuery(id+"F5.imprint","IMPRINT",FACE,{"disambiguationData":[TD([[makeQuery(id+"F5.imprint","IMPRINT",EDGE,{"derivedFrom":sQuery(id+"F5.wireOp",EDGE,"E42.MirrorCS")}),-1.0]])]});
            var Q3;
            Q3=makeQuery(id+"F5.imprint","IMPRINT",FACE,{"disambiguationData":[TD([[makeQuery(id+"F5.imprint","IMPRINT",EDGE,{"derivedFrom":sQuery(id+"F5.wireOp",EDGE,"E41.MirrorCS")}),-1.0]])]});
            var Q4;
            Q4=makeQuery(id+"F5.imprint","IMPRINT",FACE,{"disambiguationData":[TD([[makeQuery(id+"F5.imprint","IMPRINT",EDGE,{"derivedFrom":sQuery(id+"F5.wireOp",EDGE,"E40.MirrorCS")}),1.0]])]});
            var Q5;
            Q5=makeQuery(id+"F5.imprint","IMPRINT",FACE,{"disambiguationData":[TD([[makeQuery(id+"F5.imprint","IMPRINT",EDGE,{"derivedFrom":sQuery(id+"F5.wireOp",EDGE,"E39.MirrorCS")}),-1.0]])]});
            var Q6;
            Q6=makeQuery(id+"F5.imprint","IMPRINT",FACE,{"disambiguationData":[TD([[makeQuery(id+"F5.imprint","IMPRINT",EDGE,{"derivedFrom":sQuery(id+"F5.wireOp",EDGE,"E27")}),1.0]])]});
            var Q7;
            Q7=makeQuery(id+"F5.imprint","IMPRINT",FACE,{"disambiguationData":[TD([[makeQuery(id+"F5.imprint","IMPRINT",EDGE,{"derivedFrom":sQuery(id+"F5.wireOp",EDGE,"E28")}),-1.0]])]});
            var Q8;
            Q8=makeQuery(id+"F5.imprint","IMPRINT",FACE,{"disambiguationData":[TD([[makeQuery(id+"F5.imprint","IMPRINT",EDGE,{"derivedFrom":sQuery(id+"F5.wireOp",EDGE,"E29")}),1.0]])]});
            var Q9;
            Q9=makeQuery(id+"F5.imprint","IMPRINT",FACE,{"disambiguationData":[TD([[makeQuery(id+"F5.imprint","IMPRINT",EDGE,{"derivedFrom":sQuery(id+"F5.wireOp",EDGE,"E30")}),-1.0]])]});
            var Q10;
            Q10=makeQuery(id+"F5.imprint","IMPRINT",FACE,{"disambiguationData":[TD([[makeQuery(id+"F5.imprint","IMPRINT",EDGE,{"derivedFrom":sQuery(id+"F5.wireOp",EDGE,"E31")}),-1.0]])]});
            var Q11;
            Q11=makeQuery(id+"F5.imprint","IMPRINT",FACE,{"disambiguationData":[TD([[makeQuery(id+"F5.imprint","IMPRINT",EDGE,{"derivedFrom":sQuery(id+"F5.wireOp",EDGE,"E32")}),-1.0]])]});
            var Q12;
            Q12=makeQuery(id+"F5.imprint","IMPRINT",FACE,{"disambiguationData":[TD([[makeQuery(id+"F5.imprint","IMPRINT",EDGE,{"derivedFrom":sQuery(id+"F5.wireOp",EDGE,"E33")}),-1.0]])]});
            var Q13;
            Q13=makeQuery(id+"F5.imprint","IMPRINT",FACE,{"disambiguationData":[TD([[makeQuery(id+"F5.imprint","IMPRINT",EDGE,{"derivedFrom":sQuery(id+"F5.wireOp",EDGE,"E34.MirrorCS")}),-1.0]])]});
            var Q14;
            Q14=makeQuery(id+"F5.imprint","IMPRINT",FACE,{"disambiguationData":[TD([[makeQuery(id+"F5.imprint","IMPRINT",EDGE,{"derivedFrom":sQuery(id+"F5.wireOp",EDGE,"E35.MirrorCS")}),-1.0]])]});
            var Q15;
            Q15=makeQuery(id+"F5.imprint","IMPRINT",FACE,{"disambiguationData":[TD([[makeQuery(id+"F5.imprint","IMPRINT",EDGE,{"derivedFrom":sQuery(id+"F5.wireOp",EDGE,"E36.MirrorCS")}),-1.0]])]});
            var Q16;
            Q16=makeQuery(id+"F5.imprint","IMPRINT",FACE,{"disambiguationData":[TD([[makeQuery(id+"F5.imprint","IMPRINT",EDGE,{"derivedFrom":sQuery(id+"F5.wireOp",EDGE,"E37.MirrorCS")}),1.0]])]});
            var Q17;
            Q17=makeQuery(id+"F5.imprint","IMPRINT",FACE,{"disambiguationData":[TD([[makeQuery(id+"F5.imprint","IMPRINT",EDGE,{"derivedFrom":sQuery(id+"F5.wireOp",EDGE,"E38.MirrorCS")}),-1.0]])]});
            var Q18;
            Q18=makeQuery(id+"F5.imprint","IMPRINT",FACE,{"disambiguationData":[TD([[makeQuery(id+"F5.imprint","IMPRINT",EDGE,{"derivedFrom":sQuery(id+"F5.wireOp",EDGE,"E49")}),-1.0]])]});
            var Q19;
            Q19=makeQuery(id+"F5.imprint","IMPRINT",FACE,{"disambiguationData":[TD([[makeQuery(id+"F5.imprint","IMPRINT",EDGE,{"derivedFrom":sQuery(id+"F5.wireOp",EDGE,"E48.MirrorCS")}),-1.0]])]});
            var Q20;
            Q20=makeQuery(id+"F5.imprint","IMPRINT",FACE,{"disambiguationData":[TD([[makeQuery(id+"F5.imprint","IMPRINT",EDGE,{"derivedFrom":sQuery(id+"F5.wireOp",EDGE,"E47.MirrorCS")}),1.0]])]});
            var Q21;
            Q21=makeQuery(id+"F5.imprint","IMPRINT",FACE,{"disambiguationData":[TD([[makeQuery(id+"F5.imprint","IMPRINT",EDGE,{"derivedFrom":sQuery(id+"F5.wireOp",EDGE,"E46.MirrorCS")}),-1.0]])]});
            var Q22;
            Q22=makeQuery(id+"F5.imprint","IMPRINT",FACE,{"disambiguationData":[TD([[makeQuery(id+"F5.imprint","IMPRINT",EDGE,{"derivedFrom":sQuery(id+"F5.wireOp",EDGE,"E45.MirrorCS")}),-1.0]])]});
            var Q23;
            Q23=makeQuery(id+"F5.imprint","IMPRINT",FACE,{"disambiguationData":[TD([[makeQuery(id+"F5.imprint","IMPRINT",EDGE,{"derivedFrom":sQuery(id+"F5.wireOp",EDGE,"E44.MirrorCS")}),-1.0]])]});
            extrude(context, id + "F12", {"entities" : qUnion([Q0, Q1, Q2, Q3, Q4, Q5, Q6, Q7, Q8, Q9, Q10, Q11, Q12, Q13, Q14, Q15, Q16, Q17, Q18, Q19, Q20, Q21, Q22, Q23]), "operationType" : NewBodyOperationType.ADD, "depth" : 2 * mm});
        }
        {
            var Q0;
            {var subQ0=sQuery(id+"F6.wireOp",EDGE,"E164");Q0=makeQuery(id+"F6.imprint","IMPRINT",FACE,{"disambiguationData":[TD([[makeQuery(id+"F6.imprint","IMPRINT",EDGE,{"derivedFrom":subQ0}),-1.0]])]});}
            var Q1;
            {var subQ0=sQuery(id+"F6.wireOp",EDGE,"E152");Q1=makeQuery(id+"F6.imprint","IMPRINT",FACE,{"disambiguationData":[TD([[makeQuery(id+"F6.imprint","IMPRINT",EDGE,{"derivedFrom":subQ0}),1.0]])]});}
            var Q2;
            Q2=sQuery(id+"F6.wireOp",EDGE,"E161");
            revolve(context, id + "F13", {"operationType" : NewBodyOperationType.ADD, "entities" : qUnion([Q0, Q1]), "axis" : qUnion([Q2]), "revolveType" : RevolveType.SYMMETRIC, "angle" : 315 * degree});
        }
        {
            var Q0;
            {var subQ3=sQuery(id+"F6.wireOp",EDGE,"E157");Q0=makeQuery(id+"F6.imprint","IMPRINT",FACE,{"disambiguationData":[TD([[makeQuery(id+"F6.imprint","IMPRINT",EDGE,{"derivedFrom":subQ3}),1.0]])]});}
            var Q1;
            Q1=sQuery(id+"F6.wireOp",EDGE,"E161");
            revolve(context, id + "F14", {"operationType" : NewBodyOperationType.ADD, "entities" : qUnion([Q0]), "axis" : qUnion([Q1]), "revolveType" : RevolveType.FULL});
        }
        {
            var Q0;
            Q0=makeQuery(id+"F8.imprint","IMPRINT",FACE,{"disambiguationData":[TD([[makeQuery(id+"F8.imprint","IMPRINT",EDGE,{"derivedFrom":sQuery(id+"F8.wireOp",EDGE,"E226")}),-1.0]])]});
            extrude(context, id + "F15", {"entities" : qUnion([Q0]), "operationType" : NewBodyOperationType.ADD, "depth" : 2.5 * mm});
        }
        {
            var Q0;
            Q0=makeQuery(id+"F7.imprint","IMPRINT",FACE,{"disambiguationData":[TD([[makeQuery(id+"F7.imprint","IMPRINT",EDGE,{"derivedFrom":sQuery(id+"F7.wireOp",EDGE,"E200")}),-1.0]])]});
            extrude(context, id + "F16", {"entities" : qUnion([Q0]), "operationType" : NewBodyOperationType.ADD, "oppositeDirection" : true, "depth" : 2.5 * mm});
        }
        {
            var Q0;
            Q0=makeQuery(id+"F9.imprint","IMPRINT",FACE,{"disambiguationData":[TD([[makeQuery(id+"F9.imprint","IMPRINT",EDGE,{"derivedFrom":sQuery(id+"F9.wireOp",EDGE,"E236.MirrorCS")}),1.0]])]});
            var Q1;
            {var subQ1=sQuery(id+"F9.wireOp",EDGE,"E240.bottom");Q1=makeQuery(id+"F9.imprint","IMPRINT",FACE,{"disambiguationData":[TD([[makeQuery(id+"F9.imprint","IMPRINT",EDGE,{"derivedFrom":subQ1}),1.0]])]});}
            var Q2;
            {var subQ5=sQuery(id+"F9.wireOp",EDGE,"E242");Q2=makeQuery(id+"F9.imprint","IMPRINT",FACE,{"disambiguationData":[TD([[makeQuery(id+"F9.imprint","IMPRINT",EDGE,{"derivedFrom":subQ5}),-1.0]])]});}
            var Q3;
            {var subQ0=sQuery(id+"F9.wireOp",EDGE,"E251.0");Q3=makeQuery(id+"F9.imprint","IMPRINT",FACE,{"disambiguationData":[TD([[makeQuery(id+"F9.imprint","IMPRINT",EDGE,{"derivedFrom":subQ0}),1.0]])]});}
            extrude(context, id + "F17", {"entities" : qUnion([Q0, Q1, Q2, Q3]), "operationType" : NewBodyOperationType.ADD, "depth" : 2.5 * mm});
        }
        {
            var Q0;
            {var subQ3=sQuery(id+"F10.wireOp",EDGE,"E254.MirrorCS");Q0=makeQuery(id+"F10.imprint","IMPRINT",FACE,{"disambiguationData":[TD([[makeQuery(id+"F10.imprint","IMPRINT",EDGE,{"derivedFrom":subQ3}),1.0]])]});}
            var Q1;
            {var subQ7=sQuery(id+"F10.wireOp",EDGE,"E270.0");Q1=makeQuery(id+"F10.imprint","IMPRINT",FACE,{"disambiguationData":[TD([[makeQuery(id+"F10.imprint","IMPRINT",EDGE,{"derivedFrom":subQ7}),-1.0]])]});}
            extrude(context, id + "F18", {"entities" : qUnion([Q0, Q1]), "operationType" : NewBodyOperationType.ADD, "oppositeDirection" : true, "depth" : 2.5 * mm});
        }
        {
            var Q0;
            {var subQ4=sQuery(id+"F9.wireOp",EDGE,"E242");Q0=makeQuery(id+"F9.imprint","IMPRINT",FACE,{"disambiguationData":[TD([[makeQuery(id+"F9.imprint","IMPRINT",EDGE,{"derivedFrom":subQ4}),1.0]])]});}
            var Q1;
            {var subQ0=sQuery(id+"F9.wireOp",EDGE,"6jEM1cKR-Vwea-ILg7-sG8q-rrc46WkZxeoR");Q1=makeQuery(id+"F9.imprint","IMPRINT",FACE,{"disambiguationData":[TD([[makeQuery(id+"F9.imprint","IMPRINT",EDGE,{"derivedFrom":subQ0}),-1.0]])]});}
            var Q2;
            {var subQ0=sQuery(id+"F9.wireOp",EDGE,"E248");Q2=makeQuery(id+"F9.imprint","IMPRINT",FACE,{"disambiguationData":[TD([[makeQuery(id+"F9.imprint","IMPRINT",EDGE,{"derivedFrom":subQ0}),1.0]])]});}
            extrude(context, id + "F19", {"entities" : qUnion([Q0, Q1, Q2]), "operationType" : NewBodyOperationType.ADD, "depth" : 14 * mm});
        }
        {
            var Q0;
            {var subQ0=sQuery(id+"F10.wireOp",EDGE,"E266");Q0=makeQuery(id+"F10.imprint","IMPRINT",FACE,{"disambiguationData":[TD([[makeQuery(id+"F10.imprint","IMPRINT",EDGE,{"derivedFrom":subQ0}),1.0]])]});}
            var Q1;
            {var subQ7=sQuery(id+"F10.wireOp",EDGE,"E270.0");Q1=makeQuery(id+"F10.imprint","IMPRINT",FACE,{"disambiguationData":[TD([[makeQuery(id+"F10.imprint","IMPRINT",EDGE,{"derivedFrom":subQ7}),-1.0]])]});}
            extrude(context, id + "F20", {"entities" : qUnion([Q0, Q1]), "operationType" : NewBodyOperationType.ADD, "depth" : 10 * mm});
        }
        {
            var Q0;
            {var subQ0=sQuery(id+"F5.wireOp",EDGE,"E145");var subQ1=sQuery(id+"F5.wireOp",EDGE,"E69.MirrorCS");var subQ2=sQuery(id+"F5.wireOp",EDGE,"E46.MirrorCS");var subQ3=makeQuery(id+"F12.opExtrude","CAP_FACE",FACE,{"disambiguationData":[OSD([subQ2,subQ1,sQuery(id+"F5.wireOp",EDGE,"E117"),subQ0])],"isStart":true});var subQ4=sQuery(id+"F8.wireOp",EDGE,"E231");var subQ5=sQuery(id+"F8.wireOp",EDGE,"E230");var subQ6=sQuery(id+"F8.wireOp",EDGE,"E229");var subQ7=sQuery(id+"F8.wireOp",EDGE,"E228");var subQ8=sQuery(id+"F8.wireOp",EDGE,"E227");var subQ9=sQuery(id+"F8.wireOp",EDGE,"E226");var subQ10=makeQuery(id+"F15.opExtrude","CAP_FACE",FACE,{"disambiguationData":[OSD([subQ9,subQ8,subQ7,subQ6,subQ5,subQ4])],"isStart":false});var subQ11=sQuery(id+"F5.wireOp",EDGE,"E146");var subQ12=sQuery(id+"F5.wireOp",EDGE,"E68.MirrorCS");var subQ13=sQuery(id+"F5.wireOp",EDGE,"E45.MirrorCS");var subQ14=makeQuery(id+"F12.opExtrude","CAP_FACE",FACE,{"disambiguationData":[OSD([subQ13,subQ12,sQuery(id+"F5.wireOp",EDGE,"E120"),subQ11])],"isStart":true});var subQ15=makeQuery(id+"F14.opRevolve","SWEPT_FACE",FACE,{"disambiguationData":[OSD([sQuery(id+"F6.wireOp",EDGE,"E157")])]});var subQ16=sQuery(id+"F5.wireOp",EDGE,"E147");var subQ17=sQuery(id+"F5.wireOp",EDGE,"E74");var subQ18=sQuery(id+"F5.wireOp",EDGE,"E44.MirrorCS");var subQ19=makeQuery(id+"F12.opExtrude","CAP_FACE",FACE,{"disambiguationData":[OSD([subQ18,subQ17,sQuery(id+"F5.wireOp",EDGE,"E121"),subQ16])],"isStart":true});var subQ20=sQuery(id+"F6.wireOp",EDGE,"E164");var subQ21=sQuery(id+"F6.wireOp",EDGE,"E152");var subQ22=sQuery(id+"F6.wireOp",EDGE,"E151");var subQ23=sQuery(id+"F6.wireOp",EDGE,"E150");var subQ24=makeQuery(id+"F13.opRevolve","CAP_FACE",FACE,{"disambiguationData":[OSD([subQ23,subQ22,subQ21,subQ20])],"isStart":false});var subQ25=sQuery(id+"F5.wireOp",EDGE,"E125");var subQ26=sQuery(id+"F5.wireOp",EDGE,"E66.MirrorCS");var subQ27=sQuery(id+"F5.wireOp",EDGE,"E43.MirrorCS");var subQ28=makeQuery(id+"F12.opExtrude","CAP_FACE",FACE,{"disambiguationData":[OSD([subQ27,subQ26,sQuery(id+"F5.wireOp",EDGE,"E77"),subQ25])],"isStart":true});var subQ29=sQuery(id+"F5.wireOp",EDGE,"E126");var subQ30=sQuery(id+"F5.wireOp",EDGE,"E65.MirrorCS");var subQ31=sQuery(id+"F5.wireOp",EDGE,"E42.MirrorCS");var subQ32=makeQuery(id+"F12.opExtrude","CAP_FACE",FACE,{"disambiguationData":[OSD([subQ31,subQ30,sQuery(id+"F5.wireOp",EDGE,"E79"),subQ29])],"isStart":true});var subQ33=sQuery(id+"F5.wireOp",EDGE,"E127");var subQ34=sQuery(id+"F5.wireOp",EDGE,"E64.MirrorCS");var subQ35=sQuery(id+"F5.wireOp",EDGE,"E41.MirrorCS");var subQ36=makeQuery(id+"F12.opExtrude","CAP_FACE",FACE,{"disambiguationData":[OSD([subQ35,subQ34,sQuery(id+"F5.wireOp",EDGE,"E81"),subQ33])],"isStart":true});var subQ37=sQuery(id+"F5.wireOp",EDGE,"E128");var subQ38=sQuery(id+"F5.wireOp",EDGE,"E63.MirrorCS");var subQ39=sQuery(id+"F5.wireOp",EDGE,"E40.MirrorCS");var subQ40=makeQuery(id+"F12.opExtrude","CAP_FACE",FACE,{"disambiguationData":[OSD([subQ39,subQ38,sQuery(id+"F5.wireOp",EDGE,"E83"),subQ37])],"isStart":true});var subQ41=sQuery(id+"F5.wireOp",EDGE,"E129");var subQ42=sQuery(id+"F5.wireOp",EDGE,"E51");var subQ43=sQuery(id+"F5.wireOp",EDGE,"E39.MirrorCS");var subQ44=makeQuery(id+"F12.opExtrude","CAP_FACE",FACE,{"disambiguationData":[OSD([subQ43,subQ42,sQuery(id+"F5.wireOp",EDGE,"E85"),subQ41])],"isStart":true});var subQ45=sQuery(id+"F5.wireOp",EDGE,"E141");var subQ46=sQuery(id+"F5.wireOp",EDGE,"E73");var subQ47=sQuery(id+"F5.wireOp",EDGE,"E38.MirrorCS");var subQ48=makeQuery(id+"F12.opExtrude","CAP_FACE",FACE,{"disambiguationData":[OSD([subQ47,subQ46,sQuery(id+"F5.wireOp",EDGE,"E109"),subQ45])],"isStart":true});var subQ49=sQuery(id+"F5.wireOp",EDGE,"E140");var subQ50=sQuery(id+"F5.wireOp",EDGE,"E62.MirrorCS");var subQ51=sQuery(id+"F5.wireOp",EDGE,"E37.MirrorCS");var subQ52=makeQuery(id+"F12.opExtrude","CAP_FACE",FACE,{"disambiguationData":[OSD([subQ51,subQ50,sQuery(id+"F5.wireOp",EDGE,"E107"),subQ49])],"isStart":true});var subQ53=sQuery(id+"F5.wireOp",EDGE,"E139");var subQ54=sQuery(id+"F5.wireOp",EDGE,"E61.MirrorCS");var subQ55=sQuery(id+"F5.wireOp",EDGE,"E36.MirrorCS");var subQ56=makeQuery(id+"F12.opExtrude","CAP_FACE",FACE,{"disambiguationData":[OSD([subQ55,subQ54,sQuery(id+"F5.wireOp",EDGE,"E105"),subQ53])],"isStart":true});var subQ57=sQuery(id+"F5.wireOp",EDGE,"E138");var subQ58=sQuery(id+"F5.wireOp",EDGE,"E60.MirrorCS");var subQ59=sQuery(id+"F5.wireOp",EDGE,"E35.MirrorCS");var subQ60=makeQuery(id+"F12.opExtrude","CAP_FACE",FACE,{"disambiguationData":[OSD([subQ59,subQ58,sQuery(id+"F5.wireOp",EDGE,"E103"),subQ57])],"isStart":true});var subQ61=sQuery(id+"F5.wireOp",EDGE,"E131");var subQ62=sQuery(id+"F5.wireOp",EDGE,"E53");var subQ63=sQuery(id+"F5.wireOp",EDGE,"E28");var subQ64=makeQuery(id+"F12.opExtrude","CAP_FACE",FACE,{"disambiguationData":[OSD([subQ63,subQ62,sQuery(id+"F5.wireOp",EDGE,"E89"),subQ61])],"isStart":true});var subQ65=makeQuery(id+"F13.opRevolve","CAP_FACE",FACE,{"disambiguationData":[OSD([subQ23,subQ22,subQ21,subQ20])],"isStart":true});var subQ66=sQuery(id+"F5.wireOp",EDGE,"E130");var subQ67=sQuery(id+"F5.wireOp",EDGE,"E52");var subQ68=sQuery(id+"F5.wireOp",EDGE,"E27");var subQ69=makeQuery(id+"F12.opExtrude","CAP_FACE",FACE,{"disambiguationData":[OSD([subQ68,subQ67,sQuery(id+"F5.wireOp",EDGE,"E87"),subQ66])],"isStart":true});var subQ70=sQuery(id+"F5.wireOp",EDGE,"E144");var subQ71=sQuery(id+"F5.wireOp",EDGE,"E143");var subQ72=sQuery(id+"F5.wireOp",EDGE,"E142");var subQ73=sQuery(id+"F5.wireOp",EDGE,"E137");var subQ74=sQuery(id+"F5.wireOp",EDGE,"E136");var subQ75=sQuery(id+"F5.wireOp",EDGE,"E135");var subQ76=sQuery(id+"F5.wireOp",EDGE,"E134");var subQ77=sQuery(id+"F5.wireOp",EDGE,"E133");var subQ78=sQuery(id+"F5.wireOp",EDGE,"E132");var subQ79=sQuery(id+"F5.wireOp",EDGE,"E124");var subQ80=sQuery(id+"F5.wireOp",EDGE,"E122");var subQ81=sQuery(id+"F5.wireOp",EDGE,"E119");var subQ82=sQuery(id+"F5.wireOp",EDGE,"E118");var subQ83=sQuery(id+"F5.wireOp",EDGE,"E116");var subQ84=sQuery(id+"F5.wireOp",EDGE,"E114");var subQ85=sQuery(id+"F5.wireOp",EDGE,"E112");var subQ86=sQuery(id+"F5.wireOp",EDGE,"E110");var subQ87=sQuery(id+"F5.wireOp",EDGE,"E108");var subQ88=sQuery(id+"F5.wireOp",EDGE,"E106");var subQ89=sQuery(id+"F5.wireOp",EDGE,"E104");var subQ90=sQuery(id+"F5.wireOp",EDGE,"E102");var subQ91=sQuery(id+"F5.wireOp",EDGE,"E100");var subQ92=sQuery(id+"F5.wireOp",EDGE,"E98");var subQ93=sQuery(id+"F5.wireOp",EDGE,"E96");var subQ94=sQuery(id+"F5.wireOp",EDGE,"E94");var subQ95=sQuery(id+"F5.wireOp",EDGE,"E92");var subQ96=sQuery(id+"F5.wireOp",EDGE,"E90");var subQ97=sQuery(id+"F5.wireOp",EDGE,"E88");var subQ98=sQuery(id+"F5.wireOp",EDGE,"E86");var subQ99=sQuery(id+"F5.wireOp",EDGE,"E84");var subQ100=sQuery(id+"F5.wireOp",EDGE,"E82");var subQ101=sQuery(id+"F5.wireOp",EDGE,"E80");var subQ102=sQuery(id+"F5.wireOp",EDGE,"E78");var subQ103=sQuery(id+"F5.wireOp",EDGE,"E76");var subQ104=sQuery(id+"F5.wireOp",EDGE,"E72.MirrorCS");var subQ105=sQuery(id+"F5.wireOp",EDGE,"E71.MirrorCS");var subQ106=sQuery(id+"F5.wireOp",EDGE,"E70.MirrorCS");var subQ107=sQuery(id+"F5.wireOp",EDGE,"E67.MirrorCS");var subQ108=sQuery(id+"F5.wireOp",EDGE,"E59.MirrorCS");var subQ109=sQuery(id+"F5.wireOp",EDGE,"E58.MirrorCS");var subQ110=sQuery(id+"F5.wireOp",EDGE,"E57");var subQ111=sQuery(id+"F5.wireOp",EDGE,"E56");var subQ112=sQuery(id+"F5.wireOp",EDGE,"E55");var subQ113=sQuery(id+"F5.wireOp",EDGE,"E54");var subQ114=sQuery(id+"F5.wireOp",EDGE,"E50");var subQ115=sQuery(id+"F5.wireOp",EDGE,"E49");var subQ116=sQuery(id+"F5.wireOp",EDGE,"E48.MirrorCS");var subQ117=sQuery(id+"F5.wireOp",EDGE,"E47.MirrorCS");var subQ118=sQuery(id+"F5.wireOp",EDGE,"E34.MirrorCS");var subQ119=sQuery(id+"F5.wireOp",EDGE,"E33");var subQ120=sQuery(id+"F5.wireOp",EDGE,"E32");var subQ121=sQuery(id+"F5.wireOp",EDGE,"E31");var subQ122=sQuery(id+"F5.wireOp",EDGE,"E30");var subQ123=sQuery(id+"F5.wireOp",EDGE,"E29");var subQ124=sQuery(id+"F5.wireOp",EDGE,"E1.0");var subQ125=makeQuery(id+"F11.opExtrude","CAP_FACE",FACE,{"disambiguationData":[OSD([subQ124,subQ68,subQ63,subQ123,subQ122,subQ121,subQ120,subQ119,subQ118,subQ59,subQ55,subQ51,subQ47,subQ43,subQ39,subQ35,subQ31,subQ27,subQ18,subQ13,subQ2,subQ117,subQ116,subQ115,subQ114,subQ42,subQ67,subQ62,subQ113,subQ112,subQ111,subQ110,subQ109,subQ108,subQ58,subQ54,subQ50,subQ38,subQ34,subQ30,subQ26,subQ107,subQ12,subQ1,subQ106,subQ105,subQ104,subQ46,subQ17,subQ103,subQ102,subQ101,subQ100,subQ99,subQ98,subQ97,subQ96,subQ95,subQ94,subQ93,subQ92,subQ91,subQ90,subQ89,subQ88,subQ87,subQ86,subQ85,subQ84,subQ83,subQ82,subQ81,subQ80,subQ79,subQ25,subQ29,subQ33,subQ37,subQ41,subQ66,subQ61,subQ78,subQ77,subQ76,subQ75,subQ74,subQ73,subQ57,subQ53,subQ49,subQ45,subQ72,subQ71,subQ70,subQ0,subQ11,subQ16])],"isStart":true});var subQ126=makeQuery(id+"F12.opExtrude","CAP_FACE",FACE,{"disambiguationData":[OSD([subQ114,subQ107,sQuery(id+"F5.wireOp",EDGE,"E123"),subQ79])],"isStart":true});var subQ127=makeQuery(id+"F12.opExtrude","CAP_FACE",FACE,{"disambiguationData":[OSD([subQ119,subQ109,sQuery(id+"F5.wireOp",EDGE,"E99"),subQ74])],"isStart":true});var subQ129=makeQuery(id+"F12.opExtrude","CAP_FACE",FACE,{"disambiguationData":[OSD([subQ123,subQ113,sQuery(id+"F5.wireOp",EDGE,"E91"),subQ78])],"isStart":true});var subQ130=makeQuery(id+"F12.opExtrude","CAP_FACE",FACE,{"disambiguationData":[OSD([subQ122,subQ112,sQuery(id+"F5.wireOp",EDGE,"E93"),subQ77])],"isStart":true});var subQ131=makeQuery(id+"F15.opExtrude","CAP_FACE",FACE,{"disambiguationData":[OSD([subQ9,subQ8,subQ7,subQ6,subQ5,subQ4])],"isStart":true});var subQ132=makeQuery(id+"F12.opExtrude","CAP_FACE",FACE,{"disambiguationData":[OSD([subQ121,subQ111,sQuery(id+"F5.wireOp",EDGE,"E95"),subQ76])],"isStart":true});var subQ133=makeQuery(id+"F15.opExtrude","SWEPT_FACE",FACE,{"disambiguationData":[OSD([subQ7])]});var subQ139=makeQuery(id+"F11.opExtrude","CAP_FACE",FACE,{"disambiguationData":[OSD([subQ124,subQ68,subQ63,subQ123,subQ122,subQ121,subQ120,subQ119,subQ118,subQ59,subQ55,subQ51,subQ47,subQ43,subQ39,subQ35,subQ31,subQ27,subQ18,subQ13,subQ2,subQ117,subQ116,subQ115,subQ114,subQ42,subQ67,subQ62,subQ113,subQ112,subQ111,subQ110,subQ109,subQ108,subQ58,subQ54,subQ50,subQ38,subQ34,subQ30,subQ26,subQ107,subQ12,subQ1,subQ106,subQ105,subQ104,subQ46,subQ17,subQ103,subQ102,subQ101,subQ100,subQ99,subQ98,subQ97,subQ96,subQ95,subQ94,subQ93,subQ92,subQ91,subQ90,subQ89,subQ88,subQ87,subQ86,subQ85,subQ84,subQ83,subQ82,subQ81,subQ80,subQ79,subQ25,subQ29,subQ33,subQ37,subQ41,subQ66,subQ61,subQ78,subQ77,subQ76,subQ75,subQ74,subQ73,subQ57,subQ53,subQ49,subQ45,subQ72,subQ71,subQ70,subQ0,subQ11,subQ16])],"isStart":false});var subQ140=makeQuery(id+"F12.opExtrude","CAP_FACE",FACE,{"disambiguationData":[OSD([subQ120,subQ110,sQuery(id+"F5.wireOp",EDGE,"E97"),subQ75])],"isStart":true});var subQ141=makeQuery(id+"F15.opExtrude","SWEPT_FACE",FACE,{"disambiguationData":[OSD([subQ4])]});var subQ142=makeQuery(id+"F12.opExtrude","CAP_FACE",FACE,{"disambiguationData":[OSD([subQ118,subQ108,sQuery(id+"F5.wireOp",EDGE,"E101"),subQ73])],"isStart":true});var subQ143=makeQuery(id+"F12.opExtrude","CAP_FACE",FACE,{"disambiguationData":[OSD([subQ117,subQ106,sQuery(id+"F5.wireOp",EDGE,"E115"),subQ70])],"isStart":true});var subQ144=makeQuery(id+"F12.opExtrude","CAP_FACE",FACE,{"disambiguationData":[OSD([subQ116,subQ105,sQuery(id+"F5.wireOp",EDGE,"E113"),subQ71])],"isStart":true});var subQ145=makeQuery(id+"F12.opExtrude","CAP_FACE",FACE,{"disambiguationData":[OSD([subQ115,subQ104,sQuery(id+"F5.wireOp",EDGE,"E111"),subQ72])],"isStart":true});var subQ146=makeQuery(id+"F14.opRevolve","SWEPT_FACE",FACE,{"disambiguationData":[OSD([subQ20])]});var subQ147=makeQuery(id+"F15.opExtrude","SWEPT_FACE",FACE,{"disambiguationData":[OSD([subQ8])]});var subQ148=makeQuery(id+"F15.opExtrude","SWEPT_FACE",FACE,{"disambiguationData":[OSD([subQ5])]});Q0=makeQuery(id+"F17.boolean.opBoolean","INTERSECT",EDGE,{"derivedFrom":[makeQuery(id+"F16.boolean.opBoolean","SPLIT",FACE,{"disambiguationData":[TD([subQ15])],"derivedFrom":makeQuery(id+"F15.boolean.opBoolean","SPLIT",FACE,{"disambiguationData":[TD([makeQuery(id+"F11.opExtrude","SWEPT_FACE",FACE,{"disambiguationData":[OSD([subQ124])]}),subQ125,subQ139,subQ69,subQ64,subQ129,subQ130,subQ132,subQ140,subQ127,subQ142,subQ60,subQ56,subQ52,subQ48,subQ44,subQ40,subQ36,subQ32,subQ28,subQ19,subQ14,subQ3,subQ143,subQ144,subQ145,subQ126,subQ65,subQ24,subQ15,subQ146,subQ131,subQ10,subQ147,subQ133,subQ148,subQ141])],"derivedFrom":makeQuery(id+"F14.boolean.opBoolean","MERGE",FACE,{"derivedFrom":[makeQuery(id+"F13.opRevolve","SWEPT_FACE",FACE,{"disambiguationData":[OSD([subQ23])]}),makeQuery(id+"F14.opRevolve","SWEPT_FACE",FACE,{"disambiguationData":[OSD([subQ23])]})]})})}),makeQuery(id+"F17.opExtrude","SWEPT_FACE",FACE,{"disambiguationData":[OSD([sQuery(id+"F9.wireOp",EDGE,"E237.MirrorCS")])]})]});}
            var Q1;
            {var subQ0=sQuery(id+"F5.wireOp",EDGE,"E145");var subQ1=sQuery(id+"F5.wireOp",EDGE,"E69.MirrorCS");var subQ2=sQuery(id+"F5.wireOp",EDGE,"E46.MirrorCS");var subQ3=makeQuery(id+"F12.opExtrude","CAP_FACE",FACE,{"disambiguationData":[OSD([subQ2,subQ1,sQuery(id+"F5.wireOp",EDGE,"E117"),subQ0])],"isStart":true});var subQ4=sQuery(id+"F8.wireOp",EDGE,"E231");var subQ5=sQuery(id+"F8.wireOp",EDGE,"E230");var subQ6=sQuery(id+"F8.wireOp",EDGE,"E229");var subQ7=sQuery(id+"F8.wireOp",EDGE,"E228");var subQ8=sQuery(id+"F8.wireOp",EDGE,"E227");var subQ9=sQuery(id+"F8.wireOp",EDGE,"E226");var subQ10=makeQuery(id+"F15.opExtrude","CAP_FACE",FACE,{"disambiguationData":[OSD([subQ9,subQ8,subQ7,subQ6,subQ5,subQ4])],"isStart":false});var subQ11=sQuery(id+"F5.wireOp",EDGE,"E146");var subQ12=sQuery(id+"F5.wireOp",EDGE,"E68.MirrorCS");var subQ13=sQuery(id+"F5.wireOp",EDGE,"E45.MirrorCS");var subQ14=makeQuery(id+"F12.opExtrude","CAP_FACE",FACE,{"disambiguationData":[OSD([subQ13,subQ12,sQuery(id+"F5.wireOp",EDGE,"E120"),subQ11])],"isStart":true});var subQ15=makeQuery(id+"F14.opRevolve","SWEPT_FACE",FACE,{"disambiguationData":[OSD([sQuery(id+"F6.wireOp",EDGE,"E157")])]});var subQ16=sQuery(id+"F5.wireOp",EDGE,"E147");var subQ17=sQuery(id+"F5.wireOp",EDGE,"E74");var subQ18=sQuery(id+"F5.wireOp",EDGE,"E44.MirrorCS");var subQ19=makeQuery(id+"F12.opExtrude","CAP_FACE",FACE,{"disambiguationData":[OSD([subQ18,subQ17,sQuery(id+"F5.wireOp",EDGE,"E121"),subQ16])],"isStart":true});var subQ20=sQuery(id+"F6.wireOp",EDGE,"E164");var subQ21=sQuery(id+"F6.wireOp",EDGE,"E152");var subQ22=sQuery(id+"F6.wireOp",EDGE,"E151");var subQ23=sQuery(id+"F6.wireOp",EDGE,"E150");var subQ24=makeQuery(id+"F13.opRevolve","CAP_FACE",FACE,{"disambiguationData":[OSD([subQ23,subQ22,subQ21,subQ20])],"isStart":false});var subQ25=sQuery(id+"F5.wireOp",EDGE,"E125");var subQ26=sQuery(id+"F5.wireOp",EDGE,"E66.MirrorCS");var subQ27=sQuery(id+"F5.wireOp",EDGE,"E43.MirrorCS");var subQ28=makeQuery(id+"F12.opExtrude","CAP_FACE",FACE,{"disambiguationData":[OSD([subQ27,subQ26,sQuery(id+"F5.wireOp",EDGE,"E77"),subQ25])],"isStart":true});var subQ29=sQuery(id+"F5.wireOp",EDGE,"E126");var subQ30=sQuery(id+"F5.wireOp",EDGE,"E65.MirrorCS");var subQ31=sQuery(id+"F5.wireOp",EDGE,"E42.MirrorCS");var subQ32=makeQuery(id+"F12.opExtrude","CAP_FACE",FACE,{"disambiguationData":[OSD([subQ31,subQ30,sQuery(id+"F5.wireOp",EDGE,"E79"),subQ29])],"isStart":true});var subQ33=sQuery(id+"F5.wireOp",EDGE,"E127");var subQ34=sQuery(id+"F5.wireOp",EDGE,"E64.MirrorCS");var subQ35=sQuery(id+"F5.wireOp",EDGE,"E41.MirrorCS");var subQ36=makeQuery(id+"F12.opExtrude","CAP_FACE",FACE,{"disambiguationData":[OSD([subQ35,subQ34,sQuery(id+"F5.wireOp",EDGE,"E81"),subQ33])],"isStart":true});var subQ37=sQuery(id+"F5.wireOp",EDGE,"E128");var subQ38=sQuery(id+"F5.wireOp",EDGE,"E63.MirrorCS");var subQ39=sQuery(id+"F5.wireOp",EDGE,"E40.MirrorCS");var subQ40=makeQuery(id+"F12.opExtrude","CAP_FACE",FACE,{"disambiguationData":[OSD([subQ39,subQ38,sQuery(id+"F5.wireOp",EDGE,"E83"),subQ37])],"isStart":true});var subQ41=sQuery(id+"F5.wireOp",EDGE,"E129");var subQ42=sQuery(id+"F5.wireOp",EDGE,"E51");var subQ43=sQuery(id+"F5.wireOp",EDGE,"E39.MirrorCS");var subQ44=makeQuery(id+"F12.opExtrude","CAP_FACE",FACE,{"disambiguationData":[OSD([subQ43,subQ42,sQuery(id+"F5.wireOp",EDGE,"E85"),subQ41])],"isStart":true});var subQ45=sQuery(id+"F5.wireOp",EDGE,"E141");var subQ46=sQuery(id+"F5.wireOp",EDGE,"E73");var subQ47=sQuery(id+"F5.wireOp",EDGE,"E38.MirrorCS");var subQ48=makeQuery(id+"F12.opExtrude","CAP_FACE",FACE,{"disambiguationData":[OSD([subQ47,subQ46,sQuery(id+"F5.wireOp",EDGE,"E109"),subQ45])],"isStart":true});var subQ49=sQuery(id+"F5.wireOp",EDGE,"E140");var subQ50=sQuery(id+"F5.wireOp",EDGE,"E62.MirrorCS");var subQ51=sQuery(id+"F5.wireOp",EDGE,"E37.MirrorCS");var subQ52=makeQuery(id+"F12.opExtrude","CAP_FACE",FACE,{"disambiguationData":[OSD([subQ51,subQ50,sQuery(id+"F5.wireOp",EDGE,"E107"),subQ49])],"isStart":true});var subQ53=sQuery(id+"F5.wireOp",EDGE,"E139");var subQ54=sQuery(id+"F5.wireOp",EDGE,"E61.MirrorCS");var subQ55=sQuery(id+"F5.wireOp",EDGE,"E36.MirrorCS");var subQ56=makeQuery(id+"F12.opExtrude","CAP_FACE",FACE,{"disambiguationData":[OSD([subQ55,subQ54,sQuery(id+"F5.wireOp",EDGE,"E105"),subQ53])],"isStart":true});var subQ57=sQuery(id+"F5.wireOp",EDGE,"E138");var subQ58=sQuery(id+"F5.wireOp",EDGE,"E60.MirrorCS");var subQ59=sQuery(id+"F5.wireOp",EDGE,"E35.MirrorCS");var subQ60=makeQuery(id+"F12.opExtrude","CAP_FACE",FACE,{"disambiguationData":[OSD([subQ59,subQ58,sQuery(id+"F5.wireOp",EDGE,"E103"),subQ57])],"isStart":true});var subQ61=sQuery(id+"F5.wireOp",EDGE,"E131");var subQ62=sQuery(id+"F5.wireOp",EDGE,"E53");var subQ63=sQuery(id+"F5.wireOp",EDGE,"E28");var subQ64=makeQuery(id+"F12.opExtrude","CAP_FACE",FACE,{"disambiguationData":[OSD([subQ63,subQ62,sQuery(id+"F5.wireOp",EDGE,"E89"),subQ61])],"isStart":true});var subQ65=makeQuery(id+"F13.opRevolve","CAP_FACE",FACE,{"disambiguationData":[OSD([subQ23,subQ22,subQ21,subQ20])],"isStart":true});var subQ66=sQuery(id+"F5.wireOp",EDGE,"E130");var subQ67=sQuery(id+"F5.wireOp",EDGE,"E52");var subQ68=sQuery(id+"F5.wireOp",EDGE,"E27");var subQ69=makeQuery(id+"F12.opExtrude","CAP_FACE",FACE,{"disambiguationData":[OSD([subQ68,subQ67,sQuery(id+"F5.wireOp",EDGE,"E87"),subQ66])],"isStart":true});var subQ70=sQuery(id+"F5.wireOp",EDGE,"E144");var subQ71=sQuery(id+"F5.wireOp",EDGE,"E143");var subQ72=sQuery(id+"F5.wireOp",EDGE,"E142");var subQ73=sQuery(id+"F5.wireOp",EDGE,"E137");var subQ74=sQuery(id+"F5.wireOp",EDGE,"E136");var subQ75=sQuery(id+"F5.wireOp",EDGE,"E135");var subQ76=sQuery(id+"F5.wireOp",EDGE,"E134");var subQ77=sQuery(id+"F5.wireOp",EDGE,"E133");var subQ78=sQuery(id+"F5.wireOp",EDGE,"E132");var subQ79=sQuery(id+"F5.wireOp",EDGE,"E124");var subQ80=sQuery(id+"F5.wireOp",EDGE,"E122");var subQ81=sQuery(id+"F5.wireOp",EDGE,"E119");var subQ82=sQuery(id+"F5.wireOp",EDGE,"E118");var subQ83=sQuery(id+"F5.wireOp",EDGE,"E116");var subQ84=sQuery(id+"F5.wireOp",EDGE,"E114");var subQ85=sQuery(id+"F5.wireOp",EDGE,"E112");var subQ86=sQuery(id+"F5.wireOp",EDGE,"E110");var subQ87=sQuery(id+"F5.wireOp",EDGE,"E108");var subQ88=sQuery(id+"F5.wireOp",EDGE,"E106");var subQ89=sQuery(id+"F5.wireOp",EDGE,"E104");var subQ90=sQuery(id+"F5.wireOp",EDGE,"E102");var subQ91=sQuery(id+"F5.wireOp",EDGE,"E100");var subQ92=sQuery(id+"F5.wireOp",EDGE,"E98");var subQ93=sQuery(id+"F5.wireOp",EDGE,"E96");var subQ94=sQuery(id+"F5.wireOp",EDGE,"E94");var subQ95=sQuery(id+"F5.wireOp",EDGE,"E92");var subQ96=sQuery(id+"F5.wireOp",EDGE,"E90");var subQ97=sQuery(id+"F5.wireOp",EDGE,"E88");var subQ98=sQuery(id+"F5.wireOp",EDGE,"E86");var subQ99=sQuery(id+"F5.wireOp",EDGE,"E84");var subQ100=sQuery(id+"F5.wireOp",EDGE,"E82");var subQ101=sQuery(id+"F5.wireOp",EDGE,"E80");var subQ102=sQuery(id+"F5.wireOp",EDGE,"E78");var subQ103=sQuery(id+"F5.wireOp",EDGE,"E76");var subQ104=sQuery(id+"F5.wireOp",EDGE,"E72.MirrorCS");var subQ105=sQuery(id+"F5.wireOp",EDGE,"E71.MirrorCS");var subQ106=sQuery(id+"F5.wireOp",EDGE,"E70.MirrorCS");var subQ107=sQuery(id+"F5.wireOp",EDGE,"E67.MirrorCS");var subQ108=sQuery(id+"F5.wireOp",EDGE,"E59.MirrorCS");var subQ109=sQuery(id+"F5.wireOp",EDGE,"E58.MirrorCS");var subQ110=sQuery(id+"F5.wireOp",EDGE,"E57");var subQ111=sQuery(id+"F5.wireOp",EDGE,"E56");var subQ112=sQuery(id+"F5.wireOp",EDGE,"E55");var subQ113=sQuery(id+"F5.wireOp",EDGE,"E54");var subQ114=sQuery(id+"F5.wireOp",EDGE,"E50");var subQ115=sQuery(id+"F5.wireOp",EDGE,"E49");var subQ116=sQuery(id+"F5.wireOp",EDGE,"E48.MirrorCS");var subQ117=sQuery(id+"F5.wireOp",EDGE,"E47.MirrorCS");var subQ118=sQuery(id+"F5.wireOp",EDGE,"E34.MirrorCS");var subQ119=sQuery(id+"F5.wireOp",EDGE,"E33");var subQ120=sQuery(id+"F5.wireOp",EDGE,"E32");var subQ121=sQuery(id+"F5.wireOp",EDGE,"E31");var subQ122=sQuery(id+"F5.wireOp",EDGE,"E30");var subQ123=sQuery(id+"F5.wireOp",EDGE,"E29");var subQ124=sQuery(id+"F5.wireOp",EDGE,"E1.0");var subQ125=makeQuery(id+"F11.opExtrude","CAP_FACE",FACE,{"disambiguationData":[OSD([subQ124,subQ68,subQ63,subQ123,subQ122,subQ121,subQ120,subQ119,subQ118,subQ59,subQ55,subQ51,subQ47,subQ43,subQ39,subQ35,subQ31,subQ27,subQ18,subQ13,subQ2,subQ117,subQ116,subQ115,subQ114,subQ42,subQ67,subQ62,subQ113,subQ112,subQ111,subQ110,subQ109,subQ108,subQ58,subQ54,subQ50,subQ38,subQ34,subQ30,subQ26,subQ107,subQ12,subQ1,subQ106,subQ105,subQ104,subQ46,subQ17,subQ103,subQ102,subQ101,subQ100,subQ99,subQ98,subQ97,subQ96,subQ95,subQ94,subQ93,subQ92,subQ91,subQ90,subQ89,subQ88,subQ87,subQ86,subQ85,subQ84,subQ83,subQ82,subQ81,subQ80,subQ79,subQ25,subQ29,subQ33,subQ37,subQ41,subQ66,subQ61,subQ78,subQ77,subQ76,subQ75,subQ74,subQ73,subQ57,subQ53,subQ49,subQ45,subQ72,subQ71,subQ70,subQ0,subQ11,subQ16])],"isStart":true});var subQ126=makeQuery(id+"F12.opExtrude","CAP_FACE",FACE,{"disambiguationData":[OSD([subQ114,subQ107,sQuery(id+"F5.wireOp",EDGE,"E123"),subQ79])],"isStart":true});var subQ127=makeQuery(id+"F12.opExtrude","CAP_FACE",FACE,{"disambiguationData":[OSD([subQ119,subQ109,sQuery(id+"F5.wireOp",EDGE,"E99"),subQ74])],"isStart":true});var subQ129=makeQuery(id+"F12.opExtrude","CAP_FACE",FACE,{"disambiguationData":[OSD([subQ123,subQ113,sQuery(id+"F5.wireOp",EDGE,"E91"),subQ78])],"isStart":true});var subQ130=makeQuery(id+"F12.opExtrude","CAP_FACE",FACE,{"disambiguationData":[OSD([subQ122,subQ112,sQuery(id+"F5.wireOp",EDGE,"E93"),subQ77])],"isStart":true});var subQ131=makeQuery(id+"F15.opExtrude","CAP_FACE",FACE,{"disambiguationData":[OSD([subQ9,subQ8,subQ7,subQ6,subQ5,subQ4])],"isStart":true});var subQ132=makeQuery(id+"F12.opExtrude","CAP_FACE",FACE,{"disambiguationData":[OSD([subQ121,subQ111,sQuery(id+"F5.wireOp",EDGE,"E95"),subQ76])],"isStart":true});var subQ133=makeQuery(id+"F15.opExtrude","SWEPT_FACE",FACE,{"disambiguationData":[OSD([subQ7])]});var subQ139=makeQuery(id+"F11.opExtrude","CAP_FACE",FACE,{"disambiguationData":[OSD([subQ124,subQ68,subQ63,subQ123,subQ122,subQ121,subQ120,subQ119,subQ118,subQ59,subQ55,subQ51,subQ47,subQ43,subQ39,subQ35,subQ31,subQ27,subQ18,subQ13,subQ2,subQ117,subQ116,subQ115,subQ114,subQ42,subQ67,subQ62,subQ113,subQ112,subQ111,subQ110,subQ109,subQ108,subQ58,subQ54,subQ50,subQ38,subQ34,subQ30,subQ26,subQ107,subQ12,subQ1,subQ106,subQ105,subQ104,subQ46,subQ17,subQ103,subQ102,subQ101,subQ100,subQ99,subQ98,subQ97,subQ96,subQ95,subQ94,subQ93,subQ92,subQ91,subQ90,subQ89,subQ88,subQ87,subQ86,subQ85,subQ84,subQ83,subQ82,subQ81,subQ80,subQ79,subQ25,subQ29,subQ33,subQ37,subQ41,subQ66,subQ61,subQ78,subQ77,subQ76,subQ75,subQ74,subQ73,subQ57,subQ53,subQ49,subQ45,subQ72,subQ71,subQ70,subQ0,subQ11,subQ16])],"isStart":false});var subQ140=makeQuery(id+"F12.opExtrude","CAP_FACE",FACE,{"disambiguationData":[OSD([subQ120,subQ110,sQuery(id+"F5.wireOp",EDGE,"E97"),subQ75])],"isStart":true});var subQ141=makeQuery(id+"F15.opExtrude","SWEPT_FACE",FACE,{"disambiguationData":[OSD([subQ4])]});var subQ142=makeQuery(id+"F12.opExtrude","CAP_FACE",FACE,{"disambiguationData":[OSD([subQ118,subQ108,sQuery(id+"F5.wireOp",EDGE,"E101"),subQ73])],"isStart":true});var subQ143=makeQuery(id+"F12.opExtrude","CAP_FACE",FACE,{"disambiguationData":[OSD([subQ117,subQ106,sQuery(id+"F5.wireOp",EDGE,"E115"),subQ70])],"isStart":true});var subQ144=makeQuery(id+"F12.opExtrude","CAP_FACE",FACE,{"disambiguationData":[OSD([subQ116,subQ105,sQuery(id+"F5.wireOp",EDGE,"E113"),subQ71])],"isStart":true});var subQ145=makeQuery(id+"F12.opExtrude","CAP_FACE",FACE,{"disambiguationData":[OSD([subQ115,subQ104,sQuery(id+"F5.wireOp",EDGE,"E111"),subQ72])],"isStart":true});var subQ146=makeQuery(id+"F14.opRevolve","SWEPT_FACE",FACE,{"disambiguationData":[OSD([subQ20])]});var subQ147=makeQuery(id+"F15.opExtrude","SWEPT_FACE",FACE,{"disambiguationData":[OSD([subQ8])]});var subQ148=makeQuery(id+"F15.opExtrude","SWEPT_FACE",FACE,{"disambiguationData":[OSD([subQ5])]});Q1=makeQuery(id+"F17.boolean.opBoolean","INTERSECT",EDGE,{"derivedFrom":[makeQuery(id+"F16.boolean.opBoolean","SPLIT",FACE,{"disambiguationData":[TD([subQ15])],"derivedFrom":makeQuery(id+"F15.boolean.opBoolean","SPLIT",FACE,{"disambiguationData":[TD([makeQuery(id+"F11.opExtrude","SWEPT_FACE",FACE,{"disambiguationData":[OSD([subQ124])]}),subQ125,subQ139,subQ69,subQ64,subQ129,subQ130,subQ132,subQ140,subQ127,subQ142,subQ60,subQ56,subQ52,subQ48,subQ44,subQ40,subQ36,subQ32,subQ28,subQ19,subQ14,subQ3,subQ143,subQ144,subQ145,subQ126,subQ65,subQ24,subQ15,subQ146,subQ131,subQ10,subQ147,subQ133,subQ148,subQ141])],"derivedFrom":makeQuery(id+"F14.boolean.opBoolean","MERGE",FACE,{"derivedFrom":[makeQuery(id+"F13.opRevolve","SWEPT_FACE",FACE,{"disambiguationData":[OSD([subQ23])]}),makeQuery(id+"F14.opRevolve","SWEPT_FACE",FACE,{"disambiguationData":[OSD([subQ23])]})]})})}),makeQuery(id+"F17.opExtrude","SWEPT_FACE",FACE,{"disambiguationData":[OSD([sQuery(id+"F9.wireOp",EDGE,"E236.MirrorCS")])]})]});}
            fillet(context, id + "F21", {"entities" : qUnion([Q0, Q1]), "radius" : 5 * mm, "tangentPropagation" : true, "allowEdgeOverflow" : false});
        }
        {
            var Q0;
            Q0=makeQuery(id+"F20.boolean.opBoolean","MERGE",EDGE,{"derivedFrom":[makeQuery(id+"F19.opExtrude","SWEPT_EDGE",EDGE,{"disambiguationData":[OSD([sQuery(id+"F9.wireOp",EDGE,"E248"),sQuery(id+"F9.wireOp",EDGE,"E249")])]}),makeQuery(id+"F20.opExtrude","SWEPT_EDGE",EDGE,{"disambiguationData":[OSD([sQuery(id+"F10.wireOp",EDGE,"E266"),sQuery(id+"F10.wireOp",EDGE,"E267")])]})]});
            var Q1;
            Q1=makeQuery(id+"F20.boolean.opBoolean","MERGE",EDGE,{"derivedFrom":[makeQuery(id+"F19.opExtrude","SWEPT_EDGE",EDGE,{"disambiguationData":[OSD([sQuery(id+"F9.wireOp",EDGE,"E249"),sQuery(id+"F9.wireOp",EDGE,"E250")])]}),makeQuery(id+"F20.opExtrude","SWEPT_EDGE",EDGE,{"disambiguationData":[OSD([sQuery(id+"F10.wireOp",EDGE,"E267"),sQuery(id+"F10.wireOp",EDGE,"E268")])]})]});
            var Q2;
            Q2=makeQuery(id+"F20.opExtrude","SWEPT_EDGE",EDGE,{"disambiguationData":[OSD([sQuery(id+"F10.wireOp",EDGE,"E255.MirrorCS"),sQuery(id+"F10.wireOp",EDGE,"E270.0")])]});
            var Q3;
            Q3=makeQuery(id+"F20.opExtrude","SWEPT_EDGE",EDGE,{"disambiguationData":[OSD([sQuery(id+"F10.wireOp",EDGE,"E254.MirrorCS"),sQuery(id+"F10.wireOp",EDGE,"E270.0")])]});
            var Q4;
            Q4=makeQuery(id+"F19.opExtrude","CAP_EDGE",EDGE,{"disambiguationData":[OSD([sQuery(id+"F9.wireOp",EDGE,"E249")])],"isStart":true});
            var Q5;
            Q5=makeQuery(id+"F19.opExtrude","CAP_EDGE",EDGE,{"disambiguationData":[OSD([sQuery(id+"F9.wireOp",EDGE,"E250")])],"isStart":true});
            var Q6;
            Q6=makeQuery(id+"F19.opExtrude","CAP_EDGE",EDGE,{"disambiguationData":[OSD([sQuery(id+"F9.wireOp",EDGE,"E248")])],"isStart":true});
            var Q7;
            {var subQ3=sQuery(id+"F7.wireOp",EDGE,"E202");var subQ4=sQuery(id+"F7.wireOp",EDGE,"E201");var subQ8=sQuery(id+"F6.wireOp",EDGE,"E150");var subQ9=makeQuery(id+"F14.opRevolve","SWEPT_FACE",FACE,{"disambiguationData":[OSD([subQ8])]});var subQ10=makeQuery(id+"F13.opRevolve","SWEPT_FACE",FACE,{"disambiguationData":[OSD([subQ8])]});var subQ11=makeQuery(id+"F16.opExtrude","SWEPT_FACE",FACE,{"disambiguationData":[OSD([subQ4])]});var subQ12=makeQuery(id+"F17.opExtrude","SWEPT_FACE",FACE,{"disambiguationData":[OSD([sQuery(id+"F9.wireOp",EDGE,"E237.MirrorCS")])]});var subQ13=sQuery(id+"F9.wireOp",EDGE,"E250");var subQ14=makeQuery(id+"F16.opExtrude","SWEPT_FACE",FACE,{"disambiguationData":[OSD([subQ3])]});var subQ15=sQuery(id+"F8.wireOp",EDGE,"E228");var subQ16=makeQuery(id+"F15.opExtrude","SWEPT_FACE",FACE,{"disambiguationData":[OSD([subQ15])]});var subQ17=sQuery(id+"F5.wireOp",EDGE,"E145");var subQ18=sQuery(id+"F5.wireOp",EDGE,"E69.MirrorCS");var subQ19=sQuery(id+"F5.wireOp",EDGE,"E46.MirrorCS");var subQ20=makeQuery(id+"F12.opExtrude","CAP_FACE",FACE,{"disambiguationData":[OSD([subQ19,subQ18,sQuery(id+"F5.wireOp",EDGE,"E117"),subQ17])],"isStart":true});var subQ21=sQuery(id+"F8.wireOp",EDGE,"E231");var subQ22=sQuery(id+"F8.wireOp",EDGE,"E230");var subQ23=sQuery(id+"F8.wireOp",EDGE,"E229");var subQ24=sQuery(id+"F8.wireOp",EDGE,"E227");var subQ25=sQuery(id+"F8.wireOp",EDGE,"E226");var subQ26=makeQuery(id+"F15.opExtrude","CAP_FACE",FACE,{"disambiguationData":[OSD([subQ25,subQ24,subQ15,subQ23,subQ22,subQ21])],"isStart":false});var subQ27=sQuery(id+"F5.wireOp",EDGE,"E146");var subQ28=sQuery(id+"F5.wireOp",EDGE,"E68.MirrorCS");var subQ29=sQuery(id+"F5.wireOp",EDGE,"E45.MirrorCS");var subQ30=makeQuery(id+"F12.opExtrude","CAP_FACE",FACE,{"disambiguationData":[OSD([subQ29,subQ28,sQuery(id+"F5.wireOp",EDGE,"E120"),subQ27])],"isStart":true});var subQ31=makeQuery(id+"F14.opRevolve","SWEPT_FACE",FACE,{"disambiguationData":[OSD([sQuery(id+"F6.wireOp",EDGE,"E157")])]});var subQ32=sQuery(id+"F5.wireOp",EDGE,"E147");var subQ33=sQuery(id+"F5.wireOp",EDGE,"E74");var subQ34=sQuery(id+"F5.wireOp",EDGE,"E44.MirrorCS");var subQ35=makeQuery(id+"F12.opExtrude","CAP_FACE",FACE,{"disambiguationData":[OSD([subQ34,subQ33,sQuery(id+"F5.wireOp",EDGE,"E121"),subQ32])],"isStart":true});var subQ36=sQuery(id+"F6.wireOp",EDGE,"E164");var subQ37=sQuery(id+"F6.wireOp",EDGE,"E152");var subQ38=sQuery(id+"F6.wireOp",EDGE,"E151");var subQ39=makeQuery(id+"F13.opRevolve","CAP_FACE",FACE,{"disambiguationData":[OSD([subQ8,subQ38,subQ37,subQ36])],"isStart":false});var subQ40=sQuery(id+"F5.wireOp",EDGE,"E125");var subQ41=sQuery(id+"F5.wireOp",EDGE,"E66.MirrorCS");var subQ42=sQuery(id+"F5.wireOp",EDGE,"E43.MirrorCS");var subQ43=makeQuery(id+"F12.opExtrude","CAP_FACE",FACE,{"disambiguationData":[OSD([subQ42,subQ41,sQuery(id+"F5.wireOp",EDGE,"E77"),subQ40])],"isStart":true});var subQ44=sQuery(id+"F5.wireOp",EDGE,"E126");var subQ45=sQuery(id+"F5.wireOp",EDGE,"E65.MirrorCS");var subQ46=sQuery(id+"F5.wireOp",EDGE,"E42.MirrorCS");var subQ47=makeQuery(id+"F12.opExtrude","CAP_FACE",FACE,{"disambiguationData":[OSD([subQ46,subQ45,sQuery(id+"F5.wireOp",EDGE,"E79"),subQ44])],"isStart":true});var subQ48=sQuery(id+"F5.wireOp",EDGE,"E127");var subQ49=sQuery(id+"F5.wireOp",EDGE,"E64.MirrorCS");var subQ50=sQuery(id+"F5.wireOp",EDGE,"E41.MirrorCS");var subQ51=makeQuery(id+"F12.opExtrude","CAP_FACE",FACE,{"disambiguationData":[OSD([subQ50,subQ49,sQuery(id+"F5.wireOp",EDGE,"E81"),subQ48])],"isStart":true});var subQ52=sQuery(id+"F5.wireOp",EDGE,"E128");var subQ53=sQuery(id+"F5.wireOp",EDGE,"E63.MirrorCS");var subQ54=sQuery(id+"F5.wireOp",EDGE,"E40.MirrorCS");var subQ55=makeQuery(id+"F12.opExtrude","CAP_FACE",FACE,{"disambiguationData":[OSD([subQ54,subQ53,sQuery(id+"F5.wireOp",EDGE,"E83"),subQ52])],"isStart":true});var subQ56=sQuery(id+"F5.wireOp",EDGE,"E129");var subQ57=sQuery(id+"F5.wireOp",EDGE,"E51");var subQ58=sQuery(id+"F5.wireOp",EDGE,"E39.MirrorCS");var subQ59=makeQuery(id+"F12.opExtrude","CAP_FACE",FACE,{"disambiguationData":[OSD([subQ58,subQ57,sQuery(id+"F5.wireOp",EDGE,"E85"),subQ56])],"isStart":true});var subQ60=sQuery(id+"F5.wireOp",EDGE,"E141");var subQ61=sQuery(id+"F5.wireOp",EDGE,"E73");var subQ62=sQuery(id+"F5.wireOp",EDGE,"E38.MirrorCS");var subQ63=makeQuery(id+"F12.opExtrude","CAP_FACE",FACE,{"disambiguationData":[OSD([subQ62,subQ61,sQuery(id+"F5.wireOp",EDGE,"E109"),subQ60])],"isStart":true});var subQ64=sQuery(id+"F5.wireOp",EDGE,"E140");var subQ65=sQuery(id+"F5.wireOp",EDGE,"E62.MirrorCS");var subQ66=sQuery(id+"F5.wireOp",EDGE,"E37.MirrorCS");var subQ67=makeQuery(id+"F12.opExtrude","CAP_FACE",FACE,{"disambiguationData":[OSD([subQ66,subQ65,sQuery(id+"F5.wireOp",EDGE,"E107"),subQ64])],"isStart":true});var subQ68=sQuery(id+"F5.wireOp",EDGE,"E139");var subQ69=sQuery(id+"F5.wireOp",EDGE,"E61.MirrorCS");var subQ70=sQuery(id+"F5.wireOp",EDGE,"E36.MirrorCS");var subQ71=makeQuery(id+"F12.opExtrude","CAP_FACE",FACE,{"disambiguationData":[OSD([subQ70,subQ69,sQuery(id+"F5.wireOp",EDGE,"E105"),subQ68])],"isStart":true});var subQ72=sQuery(id+"F5.wireOp",EDGE,"E138");var subQ73=sQuery(id+"F5.wireOp",EDGE,"E60.MirrorCS");var subQ74=sQuery(id+"F5.wireOp",EDGE,"E35.MirrorCS");var subQ75=makeQuery(id+"F12.opExtrude","CAP_FACE",FACE,{"disambiguationData":[OSD([subQ74,subQ73,sQuery(id+"F5.wireOp",EDGE,"E103"),subQ72])],"isStart":true});var subQ76=sQuery(id+"F5.wireOp",EDGE,"E131");var subQ77=sQuery(id+"F5.wireOp",EDGE,"E53");var subQ78=sQuery(id+"F5.wireOp",EDGE,"E28");var subQ79=makeQuery(id+"F12.opExtrude","CAP_FACE",FACE,{"disambiguationData":[OSD([subQ78,subQ77,sQuery(id+"F5.wireOp",EDGE,"E89"),subQ76])],"isStart":true});var subQ80=makeQuery(id+"F13.opRevolve","CAP_FACE",FACE,{"disambiguationData":[OSD([subQ8,subQ38,subQ37,subQ36])],"isStart":true});var subQ81=sQuery(id+"F5.wireOp",EDGE,"E130");var subQ82=sQuery(id+"F5.wireOp",EDGE,"E52");var subQ83=sQuery(id+"F5.wireOp",EDGE,"E27");var subQ84=makeQuery(id+"F12.opExtrude","CAP_FACE",FACE,{"disambiguationData":[OSD([subQ83,subQ82,sQuery(id+"F5.wireOp",EDGE,"E87"),subQ81])],"isStart":true});var subQ85=sQuery(id+"F5.wireOp",EDGE,"E144");var subQ86=sQuery(id+"F5.wireOp",EDGE,"E143");var subQ87=sQuery(id+"F5.wireOp",EDGE,"E142");var subQ88=sQuery(id+"F5.wireOp",EDGE,"E137");var subQ89=sQuery(id+"F5.wireOp",EDGE,"E136");var subQ90=sQuery(id+"F5.wireOp",EDGE,"E135");var subQ91=sQuery(id+"F5.wireOp",EDGE,"E134");var subQ92=sQuery(id+"F5.wireOp",EDGE,"E133");var subQ93=sQuery(id+"F5.wireOp",EDGE,"E132");var subQ94=sQuery(id+"F5.wireOp",EDGE,"E124");var subQ95=sQuery(id+"F5.wireOp",EDGE,"E122");var subQ96=sQuery(id+"F5.wireOp",EDGE,"E119");var subQ97=sQuery(id+"F5.wireOp",EDGE,"E118");var subQ98=sQuery(id+"F5.wireOp",EDGE,"E116");var subQ99=sQuery(id+"F5.wireOp",EDGE,"E114");var subQ100=sQuery(id+"F5.wireOp",EDGE,"E112");var subQ101=sQuery(id+"F5.wireOp",EDGE,"E110");var subQ102=sQuery(id+"F5.wireOp",EDGE,"E108");var subQ103=sQuery(id+"F5.wireOp",EDGE,"E106");var subQ104=sQuery(id+"F5.wireOp",EDGE,"E104");var subQ105=sQuery(id+"F5.wireOp",EDGE,"E102");var subQ106=sQuery(id+"F5.wireOp",EDGE,"E100");var subQ107=sQuery(id+"F5.wireOp",EDGE,"E98");var subQ108=sQuery(id+"F5.wireOp",EDGE,"E96");var subQ109=sQuery(id+"F5.wireOp",EDGE,"E94");var subQ110=sQuery(id+"F5.wireOp",EDGE,"E92");var subQ111=sQuery(id+"F5.wireOp",EDGE,"E90");var subQ112=sQuery(id+"F5.wireOp",EDGE,"E88");var subQ113=sQuery(id+"F5.wireOp",EDGE,"E86");var subQ114=sQuery(id+"F5.wireOp",EDGE,"E84");var subQ115=sQuery(id+"F5.wireOp",EDGE,"E82");var subQ116=sQuery(id+"F5.wireOp",EDGE,"E80");var subQ117=sQuery(id+"F5.wireOp",EDGE,"E78");var subQ118=sQuery(id+"F5.wireOp",EDGE,"E76");var subQ119=sQuery(id+"F5.wireOp",EDGE,"E72.MirrorCS");var subQ120=sQuery(id+"F5.wireOp",EDGE,"E71.MirrorCS");var subQ121=sQuery(id+"F5.wireOp",EDGE,"E70.MirrorCS");var subQ122=sQuery(id+"F5.wireOp",EDGE,"E67.MirrorCS");var subQ123=sQuery(id+"F5.wireOp",EDGE,"E59.MirrorCS");var subQ124=sQuery(id+"F5.wireOp",EDGE,"E58.MirrorCS");var subQ125=sQuery(id+"F5.wireOp",EDGE,"E57");var subQ126=sQuery(id+"F5.wireOp",EDGE,"E56");var subQ127=sQuery(id+"F5.wireOp",EDGE,"E55");var subQ128=sQuery(id+"F5.wireOp",EDGE,"E54");var subQ129=sQuery(id+"F5.wireOp",EDGE,"E50");var subQ130=sQuery(id+"F5.wireOp",EDGE,"E49");var subQ131=sQuery(id+"F5.wireOp",EDGE,"E48.MirrorCS");var subQ132=sQuery(id+"F5.wireOp",EDGE,"E47.MirrorCS");var subQ133=sQuery(id+"F5.wireOp",EDGE,"E34.MirrorCS");var subQ134=sQuery(id+"F5.wireOp",EDGE,"E33");var subQ135=sQuery(id+"F5.wireOp",EDGE,"E32");var subQ136=sQuery(id+"F5.wireOp",EDGE,"E31");var subQ137=sQuery(id+"F5.wireOp",EDGE,"E30");var subQ138=sQuery(id+"F5.wireOp",EDGE,"E29");var subQ139=sQuery(id+"F5.wireOp",EDGE,"E1.0");var subQ140=makeQuery(id+"F11.opExtrude","CAP_FACE",FACE,{"disambiguationData":[OSD([subQ139,subQ83,subQ78,subQ138,subQ137,subQ136,subQ135,subQ134,subQ133,subQ74,subQ70,subQ66,subQ62,subQ58,subQ54,subQ50,subQ46,subQ42,subQ34,subQ29,subQ19,subQ132,subQ131,subQ130,subQ129,subQ57,subQ82,subQ77,subQ128,subQ127,subQ126,subQ125,subQ124,subQ123,subQ73,subQ69,subQ65,subQ53,subQ49,subQ45,subQ41,subQ122,subQ28,subQ18,subQ121,subQ120,subQ119,subQ61,subQ33,subQ118,subQ117,subQ116,subQ115,subQ114,subQ113,subQ112,subQ111,subQ110,subQ109,subQ108,subQ107,subQ106,subQ105,subQ104,subQ103,subQ102,subQ101,subQ100,subQ99,subQ98,subQ97,subQ96,subQ95,subQ94,subQ40,subQ44,subQ48,subQ52,subQ56,subQ81,subQ76,subQ93,subQ92,subQ91,subQ90,subQ89,subQ88,subQ72,subQ68,subQ64,subQ60,subQ87,subQ86,subQ85,subQ17,subQ27,subQ32])],"isStart":true});var subQ141=makeQuery(id+"F12.opExtrude","CAP_FACE",FACE,{"disambiguationData":[OSD([subQ129,subQ122,sQuery(id+"F5.wireOp",EDGE,"E123"),subQ94])],"isStart":true});var subQ142=makeQuery(id+"F12.opExtrude","CAP_FACE",FACE,{"disambiguationData":[OSD([subQ134,subQ124,sQuery(id+"F5.wireOp",EDGE,"E99"),subQ89])],"isStart":true});var subQ143=makeQuery(id+"F12.opExtrude","CAP_FACE",FACE,{"disambiguationData":[OSD([subQ138,subQ128,sQuery(id+"F5.wireOp",EDGE,"E91"),subQ93])],"isStart":true});var subQ144=makeQuery(id+"F12.opExtrude","CAP_FACE",FACE,{"disambiguationData":[OSD([subQ137,subQ127,sQuery(id+"F5.wireOp",EDGE,"E93"),subQ92])],"isStart":true});var subQ145=makeQuery(id+"F15.opExtrude","CAP_FACE",FACE,{"disambiguationData":[OSD([subQ25,subQ24,subQ15,subQ23,subQ22,subQ21])],"isStart":true});var subQ146=makeQuery(id+"F12.opExtrude","CAP_FACE",FACE,{"disambiguationData":[OSD([subQ136,subQ126,sQuery(id+"F5.wireOp",EDGE,"E95"),subQ91])],"isStart":true});var subQ147=makeQuery(id+"F11.opExtrude","CAP_FACE",FACE,{"disambiguationData":[OSD([subQ139,subQ83,subQ78,subQ138,subQ137,subQ136,subQ135,subQ134,subQ133,subQ74,subQ70,subQ66,subQ62,subQ58,subQ54,subQ50,subQ46,subQ42,subQ34,subQ29,subQ19,subQ132,subQ131,subQ130,subQ129,subQ57,subQ82,subQ77,subQ128,subQ127,subQ126,subQ125,subQ124,subQ123,subQ73,subQ69,subQ65,subQ53,subQ49,subQ45,subQ41,subQ122,subQ28,subQ18,subQ121,subQ120,subQ119,subQ61,subQ33,subQ118,subQ117,subQ116,subQ115,subQ114,subQ113,subQ112,subQ111,subQ110,subQ109,subQ108,subQ107,subQ106,subQ105,subQ104,subQ103,subQ102,subQ101,subQ100,subQ99,subQ98,subQ97,subQ96,subQ95,subQ94,subQ40,subQ44,subQ48,subQ52,subQ56,subQ81,subQ76,subQ93,subQ92,subQ91,subQ90,subQ89,subQ88,subQ72,subQ68,subQ64,subQ60,subQ87,subQ86,subQ85,subQ17,subQ27,subQ32])],"isStart":false});var subQ148=makeQuery(id+"F12.opExtrude","CAP_FACE",FACE,{"disambiguationData":[OSD([subQ135,subQ125,sQuery(id+"F5.wireOp",EDGE,"E97"),subQ90])],"isStart":true});var subQ149=makeQuery(id+"F15.opExtrude","SWEPT_FACE",FACE,{"disambiguationData":[OSD([subQ21])]});var subQ150=makeQuery(id+"F12.opExtrude","CAP_FACE",FACE,{"disambiguationData":[OSD([subQ133,subQ123,sQuery(id+"F5.wireOp",EDGE,"E101"),subQ88])],"isStart":true});var subQ151=makeQuery(id+"F12.opExtrude","CAP_FACE",FACE,{"disambiguationData":[OSD([subQ132,subQ121,sQuery(id+"F5.wireOp",EDGE,"E115"),subQ85])],"isStart":true});var subQ152=makeQuery(id+"F12.opExtrude","CAP_FACE",FACE,{"disambiguationData":[OSD([subQ131,subQ120,sQuery(id+"F5.wireOp",EDGE,"E113"),subQ86])],"isStart":true});var subQ153=makeQuery(id+"F12.opExtrude","CAP_FACE",FACE,{"disambiguationData":[OSD([subQ130,subQ119,sQuery(id+"F5.wireOp",EDGE,"E111"),subQ87])],"isStart":true});var subQ154=makeQuery(id+"F14.opRevolve","SWEPT_FACE",FACE,{"disambiguationData":[OSD([subQ36])]});var subQ155=makeQuery(id+"F15.opExtrude","SWEPT_FACE",FACE,{"disambiguationData":[OSD([subQ24])]});var subQ156=makeQuery(id+"F15.opExtrude","SWEPT_FACE",FACE,{"disambiguationData":[OSD([subQ22])]});Q7=makeQuery(id+"F21.opFillet","BLEND_EDGE",EDGE,{"blendedFrom":[makeQuery(id+"F17.boolean.opBoolean","INTERSECT",EDGE,{"derivedFrom":[makeQuery(id+"F16.boolean.opBoolean","SPLIT",FACE,{"disambiguationData":[TD([subQ31])],"derivedFrom":makeQuery(id+"F15.boolean.opBoolean","SPLIT",FACE,{"disambiguationData":[TD([makeQuery(id+"F11.opExtrude","SWEPT_FACE",FACE,{"disambiguationData":[OSD([subQ139])]}),subQ140,subQ147,subQ84,subQ79,subQ143,subQ144,subQ146,subQ148,subQ142,subQ150,subQ75,subQ71,subQ67,subQ63,subQ59,subQ55,subQ51,subQ47,subQ43,subQ35,subQ30,subQ20,subQ151,subQ152,subQ153,subQ141,subQ80,subQ39,subQ31,subQ154,subQ145,subQ26,subQ155,subQ16,subQ156,subQ149])],"derivedFrom":makeQuery(id+"F14.boolean.opBoolean","MERGE",FACE,{"derivedFrom":[subQ10,subQ9]})})}),subQ12]}),makeQuery(id+"F20.boolean.opBoolean","SPLIT",FACE,{"disambiguationData":[TD([subQ11])],"derivedFrom":makeQuery(id+"F19.boolean.opBoolean","MERGE",FACE,{"derivedFrom":[subQ16,subQ14,makeQuery(id+"F19.opExtrude","CAP_FACE",FACE,{"disambiguationData":[OSD([sQuery(id+"F9.wireOp",EDGE,"E238.MirrorCS"),sQuery(id+"F9.wireOp",EDGE,"E248"),sQuery(id+"F9.wireOp",EDGE,"E249"),subQ13,sQuery(id+"F9.wireOp",EDGE,"E251.0"),sQuery(id+"F9.wireOp",EDGE,"E251.1"),sQuery(id+"F9.wireOp",EDGE,"E251.2")])],"isStart":false})]})})],"blendedInto":[makeQuery(id+"F20.boolean.opBoolean","SPLIT",FACE,{"disambiguationData":[TD([subQ11])],"derivedFrom":makeQuery(id+"F19.boolean.opBoolean","MERGE",FACE,{"derivedFrom":[subQ16,subQ14,makeQuery(id+"F19.opExtrude","CAP_FACE",FACE,{"disambiguationData":[OSD([sQuery(id+"F9.wireOp",EDGE,"E238.MirrorCS"),sQuery(id+"F9.wireOp",EDGE,"E248"),sQuery(id+"F9.wireOp",EDGE,"E249"),subQ13,sQuery(id+"F9.wireOp",EDGE,"E251.0"),sQuery(id+"F9.wireOp",EDGE,"E251.1"),sQuery(id+"F9.wireOp",EDGE,"E251.2")])],"isStart":false})]})})]});}
            var Q8;
            {var subQ0=sQuery(id+"F8.wireOp",EDGE,"E231");var subQ1=sQuery(id+"F8.wireOp",EDGE,"E230");var subQ2=sQuery(id+"F8.wireOp",EDGE,"E229");var subQ3=sQuery(id+"F8.wireOp",EDGE,"E228");var subQ4=sQuery(id+"F8.wireOp",EDGE,"E227");var subQ5=sQuery(id+"F8.wireOp",EDGE,"E226");var subQ6=makeQuery(id+"F15.opExtrude","CAP_FACE",FACE,{"disambiguationData":[OSD([subQ5,subQ4,subQ3,subQ2,subQ1,subQ0])],"isStart":false});var subQ7=sQuery(id+"F6.wireOp",EDGE,"E150");var subQ8=makeQuery(id+"F14.opRevolve","SWEPT_FACE",FACE,{"disambiguationData":[OSD([subQ7])]});var subQ9=makeQuery(id+"F15.opExtrude","SWEPT_FACE",FACE,{"disambiguationData":[OSD([subQ4])]});var subQ10=sQuery(id+"F9.wireOp",EDGE,"E248");var subQ11=makeQuery(id+"F15.opExtrude","CAP_FACE",FACE,{"disambiguationData":[OSD([subQ5,subQ4,subQ3,subQ2,subQ1,subQ0])],"isStart":true});var subQ12=makeQuery(id+"F13.opRevolve","SWEPT_FACE",FACE,{"disambiguationData":[OSD([subQ7])]});var subQ13=makeQuery(id+"F17.opExtrude","SWEPT_FACE",FACE,{"disambiguationData":[OSD([sQuery(id+"F9.wireOp",EDGE,"E236.MirrorCS")])]});var subQ14=sQuery(id+"F7.wireOp",EDGE,"E202");var subQ15=makeQuery(id+"F16.opExtrude","SWEPT_FACE",FACE,{"disambiguationData":[OSD([subQ14])]});var subQ16=makeQuery(id+"F15.opExtrude","SWEPT_FACE",FACE,{"disambiguationData":[OSD([subQ3])]});var subQ17=sQuery(id+"F5.wireOp",EDGE,"E145");var subQ18=sQuery(id+"F5.wireOp",EDGE,"E69.MirrorCS");var subQ19=sQuery(id+"F5.wireOp",EDGE,"E46.MirrorCS");var subQ20=makeQuery(id+"F12.opExtrude","CAP_FACE",FACE,{"disambiguationData":[OSD([subQ19,subQ18,sQuery(id+"F5.wireOp",EDGE,"E117"),subQ17])],"isStart":true});var subQ21=sQuery(id+"F5.wireOp",EDGE,"E146");var subQ22=sQuery(id+"F5.wireOp",EDGE,"E68.MirrorCS");var subQ23=sQuery(id+"F5.wireOp",EDGE,"E45.MirrorCS");var subQ24=makeQuery(id+"F12.opExtrude","CAP_FACE",FACE,{"disambiguationData":[OSD([subQ23,subQ22,sQuery(id+"F5.wireOp",EDGE,"E120"),subQ21])],"isStart":true});var subQ25=makeQuery(id+"F14.opRevolve","SWEPT_FACE",FACE,{"disambiguationData":[OSD([sQuery(id+"F6.wireOp",EDGE,"E157")])]});var subQ26=sQuery(id+"F5.wireOp",EDGE,"E147");var subQ27=sQuery(id+"F5.wireOp",EDGE,"E74");var subQ28=sQuery(id+"F5.wireOp",EDGE,"E44.MirrorCS");var subQ29=makeQuery(id+"F12.opExtrude","CAP_FACE",FACE,{"disambiguationData":[OSD([subQ28,subQ27,sQuery(id+"F5.wireOp",EDGE,"E121"),subQ26])],"isStart":true});var subQ30=sQuery(id+"F6.wireOp",EDGE,"E164");var subQ31=sQuery(id+"F6.wireOp",EDGE,"E152");var subQ32=sQuery(id+"F6.wireOp",EDGE,"E151");var subQ33=makeQuery(id+"F13.opRevolve","CAP_FACE",FACE,{"disambiguationData":[OSD([subQ7,subQ32,subQ31,subQ30])],"isStart":false});var subQ34=sQuery(id+"F5.wireOp",EDGE,"E125");var subQ35=sQuery(id+"F5.wireOp",EDGE,"E66.MirrorCS");var subQ36=sQuery(id+"F5.wireOp",EDGE,"E43.MirrorCS");var subQ37=makeQuery(id+"F12.opExtrude","CAP_FACE",FACE,{"disambiguationData":[OSD([subQ36,subQ35,sQuery(id+"F5.wireOp",EDGE,"E77"),subQ34])],"isStart":true});var subQ38=sQuery(id+"F5.wireOp",EDGE,"E126");var subQ39=sQuery(id+"F5.wireOp",EDGE,"E65.MirrorCS");var subQ40=sQuery(id+"F5.wireOp",EDGE,"E42.MirrorCS");var subQ41=makeQuery(id+"F12.opExtrude","CAP_FACE",FACE,{"disambiguationData":[OSD([subQ40,subQ39,sQuery(id+"F5.wireOp",EDGE,"E79"),subQ38])],"isStart":true});var subQ42=sQuery(id+"F5.wireOp",EDGE,"E127");var subQ43=sQuery(id+"F5.wireOp",EDGE,"E64.MirrorCS");var subQ44=sQuery(id+"F5.wireOp",EDGE,"E41.MirrorCS");var subQ45=makeQuery(id+"F12.opExtrude","CAP_FACE",FACE,{"disambiguationData":[OSD([subQ44,subQ43,sQuery(id+"F5.wireOp",EDGE,"E81"),subQ42])],"isStart":true});var subQ46=sQuery(id+"F5.wireOp",EDGE,"E128");var subQ47=sQuery(id+"F5.wireOp",EDGE,"E63.MirrorCS");var subQ48=sQuery(id+"F5.wireOp",EDGE,"E40.MirrorCS");var subQ49=makeQuery(id+"F12.opExtrude","CAP_FACE",FACE,{"disambiguationData":[OSD([subQ48,subQ47,sQuery(id+"F5.wireOp",EDGE,"E83"),subQ46])],"isStart":true});var subQ50=sQuery(id+"F5.wireOp",EDGE,"E129");var subQ51=sQuery(id+"F5.wireOp",EDGE,"E51");var subQ52=sQuery(id+"F5.wireOp",EDGE,"E39.MirrorCS");var subQ53=makeQuery(id+"F12.opExtrude","CAP_FACE",FACE,{"disambiguationData":[OSD([subQ52,subQ51,sQuery(id+"F5.wireOp",EDGE,"E85"),subQ50])],"isStart":true});var subQ54=sQuery(id+"F5.wireOp",EDGE,"E141");var subQ55=sQuery(id+"F5.wireOp",EDGE,"E73");var subQ56=sQuery(id+"F5.wireOp",EDGE,"E38.MirrorCS");var subQ57=makeQuery(id+"F12.opExtrude","CAP_FACE",FACE,{"disambiguationData":[OSD([subQ56,subQ55,sQuery(id+"F5.wireOp",EDGE,"E109"),subQ54])],"isStart":true});var subQ58=sQuery(id+"F5.wireOp",EDGE,"E140");var subQ59=sQuery(id+"F5.wireOp",EDGE,"E62.MirrorCS");var subQ60=sQuery(id+"F5.wireOp",EDGE,"E37.MirrorCS");var subQ61=makeQuery(id+"F12.opExtrude","CAP_FACE",FACE,{"disambiguationData":[OSD([subQ60,subQ59,sQuery(id+"F5.wireOp",EDGE,"E107"),subQ58])],"isStart":true});var subQ62=sQuery(id+"F5.wireOp",EDGE,"E139");var subQ63=sQuery(id+"F5.wireOp",EDGE,"E61.MirrorCS");var subQ64=sQuery(id+"F5.wireOp",EDGE,"E36.MirrorCS");var subQ65=makeQuery(id+"F12.opExtrude","CAP_FACE",FACE,{"disambiguationData":[OSD([subQ64,subQ63,sQuery(id+"F5.wireOp",EDGE,"E105"),subQ62])],"isStart":true});var subQ66=sQuery(id+"F5.wireOp",EDGE,"E138");var subQ67=sQuery(id+"F5.wireOp",EDGE,"E60.MirrorCS");var subQ68=sQuery(id+"F5.wireOp",EDGE,"E35.MirrorCS");var subQ69=makeQuery(id+"F12.opExtrude","CAP_FACE",FACE,{"disambiguationData":[OSD([subQ68,subQ67,sQuery(id+"F5.wireOp",EDGE,"E103"),subQ66])],"isStart":true});var subQ70=sQuery(id+"F5.wireOp",EDGE,"E131");var subQ71=sQuery(id+"F5.wireOp",EDGE,"E53");var subQ72=sQuery(id+"F5.wireOp",EDGE,"E28");var subQ73=makeQuery(id+"F12.opExtrude","CAP_FACE",FACE,{"disambiguationData":[OSD([subQ72,subQ71,sQuery(id+"F5.wireOp",EDGE,"E89"),subQ70])],"isStart":true});var subQ74=makeQuery(id+"F13.opRevolve","CAP_FACE",FACE,{"disambiguationData":[OSD([subQ7,subQ32,subQ31,subQ30])],"isStart":true});var subQ75=sQuery(id+"F5.wireOp",EDGE,"E130");var subQ76=sQuery(id+"F5.wireOp",EDGE,"E52");var subQ77=sQuery(id+"F5.wireOp",EDGE,"E27");var subQ78=makeQuery(id+"F12.opExtrude","CAP_FACE",FACE,{"disambiguationData":[OSD([subQ77,subQ76,sQuery(id+"F5.wireOp",EDGE,"E87"),subQ75])],"isStart":true});var subQ79=sQuery(id+"F5.wireOp",EDGE,"E144");var subQ80=sQuery(id+"F5.wireOp",EDGE,"E143");var subQ81=sQuery(id+"F5.wireOp",EDGE,"E142");var subQ82=sQuery(id+"F5.wireOp",EDGE,"E137");var subQ83=sQuery(id+"F5.wireOp",EDGE,"E136");var subQ84=sQuery(id+"F5.wireOp",EDGE,"E135");var subQ85=sQuery(id+"F5.wireOp",EDGE,"E134");var subQ86=sQuery(id+"F5.wireOp",EDGE,"E133");var subQ87=sQuery(id+"F5.wireOp",EDGE,"E132");var subQ88=sQuery(id+"F5.wireOp",EDGE,"E124");var subQ89=sQuery(id+"F5.wireOp",EDGE,"E122");var subQ90=sQuery(id+"F5.wireOp",EDGE,"E119");var subQ91=sQuery(id+"F5.wireOp",EDGE,"E118");var subQ92=sQuery(id+"F5.wireOp",EDGE,"E116");var subQ93=sQuery(id+"F5.wireOp",EDGE,"E114");var subQ94=sQuery(id+"F5.wireOp",EDGE,"E112");var subQ95=sQuery(id+"F5.wireOp",EDGE,"E110");var subQ96=sQuery(id+"F5.wireOp",EDGE,"E108");var subQ97=sQuery(id+"F5.wireOp",EDGE,"E106");var subQ98=sQuery(id+"F5.wireOp",EDGE,"E104");var subQ99=sQuery(id+"F5.wireOp",EDGE,"E102");var subQ100=sQuery(id+"F5.wireOp",EDGE,"E100");var subQ101=sQuery(id+"F5.wireOp",EDGE,"E98");var subQ102=sQuery(id+"F5.wireOp",EDGE,"E96");var subQ103=sQuery(id+"F5.wireOp",EDGE,"E94");var subQ104=sQuery(id+"F5.wireOp",EDGE,"E92");var subQ105=sQuery(id+"F5.wireOp",EDGE,"E90");var subQ106=sQuery(id+"F5.wireOp",EDGE,"E88");var subQ107=sQuery(id+"F5.wireOp",EDGE,"E86");var subQ108=sQuery(id+"F5.wireOp",EDGE,"E84");var subQ109=sQuery(id+"F5.wireOp",EDGE,"E82");var subQ110=sQuery(id+"F5.wireOp",EDGE,"E80");var subQ111=sQuery(id+"F5.wireOp",EDGE,"E78");var subQ112=sQuery(id+"F5.wireOp",EDGE,"E76");var subQ113=sQuery(id+"F5.wireOp",EDGE,"E72.MirrorCS");var subQ114=sQuery(id+"F5.wireOp",EDGE,"E71.MirrorCS");var subQ115=sQuery(id+"F5.wireOp",EDGE,"E70.MirrorCS");var subQ116=sQuery(id+"F5.wireOp",EDGE,"E67.MirrorCS");var subQ117=sQuery(id+"F5.wireOp",EDGE,"E59.MirrorCS");var subQ118=sQuery(id+"F5.wireOp",EDGE,"E58.MirrorCS");var subQ119=sQuery(id+"F5.wireOp",EDGE,"E57");var subQ120=sQuery(id+"F5.wireOp",EDGE,"E56");var subQ121=sQuery(id+"F5.wireOp",EDGE,"E55");var subQ122=sQuery(id+"F5.wireOp",EDGE,"E54");var subQ123=sQuery(id+"F5.wireOp",EDGE,"E50");var subQ124=sQuery(id+"F5.wireOp",EDGE,"E49");var subQ125=sQuery(id+"F5.wireOp",EDGE,"E48.MirrorCS");var subQ126=sQuery(id+"F5.wireOp",EDGE,"E47.MirrorCS");var subQ127=sQuery(id+"F5.wireOp",EDGE,"E34.MirrorCS");var subQ128=sQuery(id+"F5.wireOp",EDGE,"E33");var subQ129=sQuery(id+"F5.wireOp",EDGE,"E32");var subQ130=sQuery(id+"F5.wireOp",EDGE,"E31");var subQ131=sQuery(id+"F5.wireOp",EDGE,"E30");var subQ132=sQuery(id+"F5.wireOp",EDGE,"E29");var subQ133=sQuery(id+"F5.wireOp",EDGE,"E1.0");var subQ134=makeQuery(id+"F11.opExtrude","CAP_FACE",FACE,{"disambiguationData":[OSD([subQ133,subQ77,subQ72,subQ132,subQ131,subQ130,subQ129,subQ128,subQ127,subQ68,subQ64,subQ60,subQ56,subQ52,subQ48,subQ44,subQ40,subQ36,subQ28,subQ23,subQ19,subQ126,subQ125,subQ124,subQ123,subQ51,subQ76,subQ71,subQ122,subQ121,subQ120,subQ119,subQ118,subQ117,subQ67,subQ63,subQ59,subQ47,subQ43,subQ39,subQ35,subQ116,subQ22,subQ18,subQ115,subQ114,subQ113,subQ55,subQ27,subQ112,subQ111,subQ110,subQ109,subQ108,subQ107,subQ106,subQ105,subQ104,subQ103,subQ102,subQ101,subQ100,subQ99,subQ98,subQ97,subQ96,subQ95,subQ94,subQ93,subQ92,subQ91,subQ90,subQ89,subQ88,subQ34,subQ38,subQ42,subQ46,subQ50,subQ75,subQ70,subQ87,subQ86,subQ85,subQ84,subQ83,subQ82,subQ66,subQ62,subQ58,subQ54,subQ81,subQ80,subQ79,subQ17,subQ21,subQ26])],"isStart":true});var subQ135=makeQuery(id+"F12.opExtrude","CAP_FACE",FACE,{"disambiguationData":[OSD([subQ123,subQ116,sQuery(id+"F5.wireOp",EDGE,"E123"),subQ88])],"isStart":true});var subQ136=makeQuery(id+"F12.opExtrude","CAP_FACE",FACE,{"disambiguationData":[OSD([subQ128,subQ118,sQuery(id+"F5.wireOp",EDGE,"E99"),subQ83])],"isStart":true});var subQ138=makeQuery(id+"F12.opExtrude","CAP_FACE",FACE,{"disambiguationData":[OSD([subQ132,subQ122,sQuery(id+"F5.wireOp",EDGE,"E91"),subQ87])],"isStart":true});var subQ139=makeQuery(id+"F12.opExtrude","CAP_FACE",FACE,{"disambiguationData":[OSD([subQ131,subQ121,sQuery(id+"F5.wireOp",EDGE,"E93"),subQ86])],"isStart":true});var subQ140=makeQuery(id+"F12.opExtrude","CAP_FACE",FACE,{"disambiguationData":[OSD([subQ130,subQ120,sQuery(id+"F5.wireOp",EDGE,"E95"),subQ85])],"isStart":true});var subQ145=makeQuery(id+"F11.opExtrude","CAP_FACE",FACE,{"disambiguationData":[OSD([subQ133,subQ77,subQ72,subQ132,subQ131,subQ130,subQ129,subQ128,subQ127,subQ68,subQ64,subQ60,subQ56,subQ52,subQ48,subQ44,subQ40,subQ36,subQ28,subQ23,subQ19,subQ126,subQ125,subQ124,subQ123,subQ51,subQ76,subQ71,subQ122,subQ121,subQ120,subQ119,subQ118,subQ117,subQ67,subQ63,subQ59,subQ47,subQ43,subQ39,subQ35,subQ116,subQ22,subQ18,subQ115,subQ114,subQ113,subQ55,subQ27,subQ112,subQ111,subQ110,subQ109,subQ108,subQ107,subQ106,subQ105,subQ104,subQ103,subQ102,subQ101,subQ100,subQ99,subQ98,subQ97,subQ96,subQ95,subQ94,subQ93,subQ92,subQ91,subQ90,subQ89,subQ88,subQ34,subQ38,subQ42,subQ46,subQ50,subQ75,subQ70,subQ87,subQ86,subQ85,subQ84,subQ83,subQ82,subQ66,subQ62,subQ58,subQ54,subQ81,subQ80,subQ79,subQ17,subQ21,subQ26])],"isStart":false});var subQ146=makeQuery(id+"F12.opExtrude","CAP_FACE",FACE,{"disambiguationData":[OSD([subQ129,subQ119,sQuery(id+"F5.wireOp",EDGE,"E97"),subQ84])],"isStart":true});var subQ147=makeQuery(id+"F15.opExtrude","SWEPT_FACE",FACE,{"disambiguationData":[OSD([subQ0])]});var subQ148=makeQuery(id+"F12.opExtrude","CAP_FACE",FACE,{"disambiguationData":[OSD([subQ127,subQ117,sQuery(id+"F5.wireOp",EDGE,"E101"),subQ82])],"isStart":true});var subQ149=makeQuery(id+"F12.opExtrude","CAP_FACE",FACE,{"disambiguationData":[OSD([subQ126,subQ115,sQuery(id+"F5.wireOp",EDGE,"E115"),subQ79])],"isStart":true});var subQ150=makeQuery(id+"F12.opExtrude","CAP_FACE",FACE,{"disambiguationData":[OSD([subQ125,subQ114,sQuery(id+"F5.wireOp",EDGE,"E113"),subQ80])],"isStart":true});var subQ151=makeQuery(id+"F12.opExtrude","CAP_FACE",FACE,{"disambiguationData":[OSD([subQ124,subQ113,sQuery(id+"F5.wireOp",EDGE,"E111"),subQ81])],"isStart":true});var subQ152=makeQuery(id+"F14.opRevolve","SWEPT_FACE",FACE,{"disambiguationData":[OSD([subQ30])]});var subQ153=makeQuery(id+"F15.opExtrude","SWEPT_FACE",FACE,{"disambiguationData":[OSD([subQ1])]});Q8=makeQuery(id+"F21.opFillet","BLEND_EDGE",EDGE,{"blendedFrom":[makeQuery(id+"F17.boolean.opBoolean","INTERSECT",EDGE,{"derivedFrom":[makeQuery(id+"F16.boolean.opBoolean","SPLIT",FACE,{"disambiguationData":[TD([subQ25])],"derivedFrom":makeQuery(id+"F15.boolean.opBoolean","SPLIT",FACE,{"disambiguationData":[TD([makeQuery(id+"F11.opExtrude","SWEPT_FACE",FACE,{"disambiguationData":[OSD([subQ133])]}),subQ134,subQ145,subQ78,subQ73,subQ138,subQ139,subQ140,subQ146,subQ136,subQ148,subQ69,subQ65,subQ61,subQ57,subQ53,subQ49,subQ45,subQ41,subQ37,subQ29,subQ24,subQ20,subQ149,subQ150,subQ151,subQ135,subQ74,subQ33,subQ25,subQ152,subQ11,subQ6,subQ9,subQ16,subQ153,subQ147])],"derivedFrom":makeQuery(id+"F14.boolean.opBoolean","MERGE",FACE,{"derivedFrom":[subQ12,subQ8]})})}),subQ13]}),makeQuery(id+"F20.boolean.opBoolean","SPLIT",FACE,{"disambiguationData":[TD([subQ9])],"derivedFrom":makeQuery(id+"F19.boolean.opBoolean","MERGE",FACE,{"derivedFrom":[subQ16,subQ15,makeQuery(id+"F19.opExtrude","CAP_FACE",FACE,{"disambiguationData":[OSD([sQuery(id+"F9.wireOp",EDGE,"E238.MirrorCS"),subQ10,sQuery(id+"F9.wireOp",EDGE,"E249"),sQuery(id+"F9.wireOp",EDGE,"E250"),sQuery(id+"F9.wireOp",EDGE,"E251.0"),sQuery(id+"F9.wireOp",EDGE,"E251.1"),sQuery(id+"F9.wireOp",EDGE,"E251.2")])],"isStart":false})]})})],"blendedInto":[makeQuery(id+"F20.boolean.opBoolean","SPLIT",FACE,{"disambiguationData":[TD([subQ9])],"derivedFrom":makeQuery(id+"F19.boolean.opBoolean","MERGE",FACE,{"derivedFrom":[subQ16,subQ15,makeQuery(id+"F19.opExtrude","CAP_FACE",FACE,{"disambiguationData":[OSD([sQuery(id+"F9.wireOp",EDGE,"E238.MirrorCS"),subQ10,sQuery(id+"F9.wireOp",EDGE,"E249"),sQuery(id+"F9.wireOp",EDGE,"E250"),sQuery(id+"F9.wireOp",EDGE,"E251.0"),sQuery(id+"F9.wireOp",EDGE,"E251.1"),sQuery(id+"F9.wireOp",EDGE,"E251.2")])],"isStart":false})]})})]});}
            fillet(context, id + "F22", {"entities" : qUnion([Q0, Q1, Q2, Q3, Q4, Q5, Q6, Q7, Q8]), "radius" : 2.6 * mm, "tangentPropagation" : true, "allowEdgeOverflow" : false});
        }
    });
